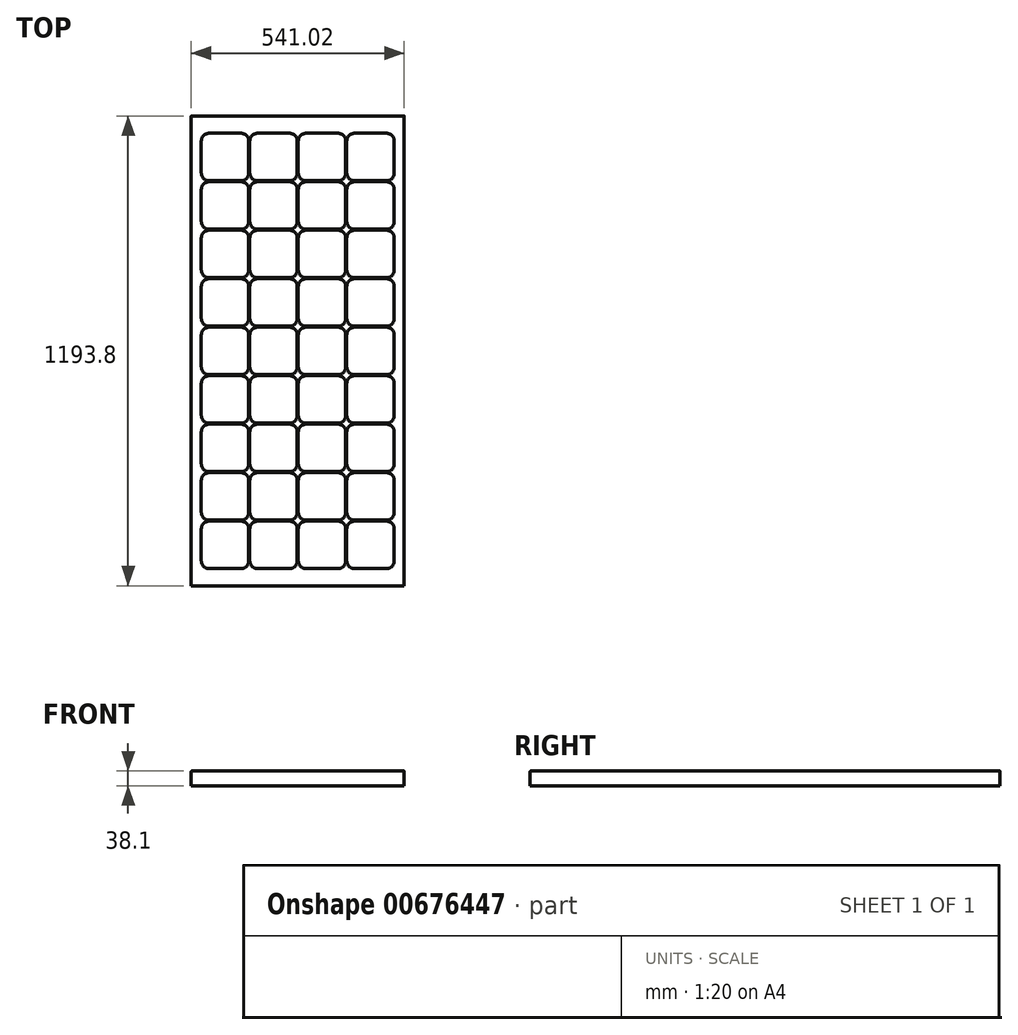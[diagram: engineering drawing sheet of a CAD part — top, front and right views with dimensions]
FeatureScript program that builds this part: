
annotation { "Feature Type Name" : "Feature", "Feature Type Description" : "" }
export const myFeature = defineFeature(function(context is Context, id is Id, definition is map)
    precondition{}
    {
        {
            var Q0;
            Q0=qCreatedBy(makeId("Top.planeOp"),FACE);
            var sketch = newSketch(context, id + "F0", { "sketchPlane" : qUnion([Q0])});
            skLineSegment(sketch, "E0.bottom", {"start": v(270.51, 596.9) * mm, "end": v(-270.5, 596.9) * mm});
            skLineSegment(sketch, "E0.top", {"start": v(270.5, -596.9) * mm, "end": v(-270.51, -596.9) * mm});
            skLineSegment(sketch, "E0.left", {"start": v(270.51, 596.9) * mm, "end": v(270.5, -596.9) * mm});
            skLineSegment(sketch, "E0.right", {"start": v(-270.5, 596.9) * mm, "end": v(-270.51, -596.9) * mm});
            skPoint(sketch, "E0.middle", {"position": v(0, 0) * mm});
            skSolve(sketch);
        }
        {
            var Q0;
            Q0=makeQuery(id+"F0.imprint","IMPRINT",FACE,{"disambiguationData":[TD([[makeQuery(id+"F0.imprint","IMPRINT",EDGE,{"derivedFrom":sQuery(id+"F0.wireOp",EDGE,"E0.bottom")}),1.0]])]});
            extrude(context, id + "F1", {"entities" : qUnion([Q0]), "depth" : 38.1 * mm, "offsetDistance" : 25.4 * mm});
        }
        {
            var Q0;
            Q0=qCreatedBy(makeId("Top.planeOp"),FACE);
            var sketch = newSketch(context, id + "F2", { "sketchPlane" : qUnion([Q0])});
            skLineSegment(sketch, "E1.bottom", {"start": v(-225.1, 553.09) * mm, "end": v(-144.46, 553.09) * mm});
            skLineSegment(sketch, "E1.top", {"start": v(-225.1, 432.44) * mm, "end": v(-144.46, 432.44) * mm});
            skLineSegment(sketch, "E1.left", {"start": v(-245.1, 533.09) * mm, "end": v(-245.1, 452.44) * mm});
            skLineSegment(sketch, "E1.right", {"start": v(-124.46, 533.09) * mm, "end": v(-124.46, 452.44) * mm});
            skPoint(sketch, "E2.visualSharp", {"position": v(-245.1, 553.09) * mm});
            skArc(sketch, "E2.filletArc", {"start": v(-225.1, 553.09) * mm, "mid": v(-239.25, 547.23) * mm, "end": v(-245.1, 533.09) * mm});
            skPoint(sketch, "E3.visualSharp", {"position": v(-124.46, 553.09) * mm});
            skArc(sketch, "E3.filletArc", {"start": v(-124.46, 533.09) * mm, "mid": v(-130.32, 547.23) * mm, "end": v(-144.46, 553.09) * mm});
            skPoint(sketch, "E4.visualSharp", {"position": v(-124.46, 432.44) * mm});
            skArc(sketch, "E4.filletArc", {"start": v(-144.46, 432.44) * mm, "mid": v(-130.32, 438.3) * mm, "end": v(-124.46, 452.44) * mm});
            skPoint(sketch, "E5.visualSharp", {"position": v(-245.1, 432.44) * mm});
            skArc(sketch, "E5.filletArc", {"start": v(-245.1, 452.44) * mm, "mid": v(-239.25, 438.3) * mm, "end": v(-225.1, 432.44) * mm});
            skLineSegment(sketch, "E6.0.1.0", {"start": v(-225.1, 429.9) * mm, "end": v(-144.46, 429.9) * mm});
            skPoint(sketch, "E6.0.1.1", {"position": v(-245.1, 309.25) * mm});
            skPoint(sketch, "E6.0.1.2", {"position": v(-124.46, 309.25) * mm});
            skPoint(sketch, "E6.0.1.3", {"position": v(-124.46, 429.9) * mm});
            skLineSegment(sketch, "E6.0.1.4", {"start": v(-225.1, 309.25) * mm, "end": v(-144.46, 309.25) * mm});
            skLineSegment(sketch, "E6.0.1.5", {"start": v(-245.1, 409.9) * mm, "end": v(-245.1, 329.25) * mm});
            skPoint(sketch, "E6.0.1.6", {"position": v(-245.1, 429.9) * mm});
            skLineSegment(sketch, "E6.0.1.7", {"start": v(-124.46, 409.9) * mm, "end": v(-124.46, 329.25) * mm});
            skArc(sketch, "E6.0.1.8", {"start": v(-124.46, 409.9) * mm, "mid": v(-130.32, 424.04) * mm, "end": v(-144.46, 429.9) * mm});
            skArc(sketch, "E6.0.1.9", {"start": v(-144.46, 309.25) * mm, "mid": v(-130.32, 315.1) * mm, "end": v(-124.46, 329.25) * mm});
            skArc(sketch, "E6.0.1.10", {"start": v(-245.1, 329.25) * mm, "mid": v(-239.25, 315.1) * mm, "end": v(-225.1, 309.25) * mm});
            skArc(sketch, "E6.0.1.11", {"start": v(-225.1, 429.9) * mm, "mid": v(-239.25, 424.04) * mm, "end": v(-245.1, 409.9) * mm});
            skLineSegment(sketch, "E6.0.2.0", {"start": v(-225.1, 306.7) * mm, "end": v(-144.46, 306.7) * mm});
            skPoint(sketch, "E6.0.2.1", {"position": v(-245.1, 186.06) * mm});
            skPoint(sketch, "E6.0.2.2", {"position": v(-124.46, 186.06) * mm});
            skPoint(sketch, "E6.0.2.3", {"position": v(-124.46, 306.7) * mm});
            skLineSegment(sketch, "E6.0.2.4", {"start": v(-225.1, 186.06) * mm, "end": v(-144.46, 186.06) * mm});
            skLineSegment(sketch, "E6.0.2.5", {"start": v(-245.1, 286.7) * mm, "end": v(-245.1, 206.06) * mm});
            skPoint(sketch, "E6.0.2.6", {"position": v(-245.1, 306.7) * mm});
            skLineSegment(sketch, "E6.0.2.7", {"start": v(-124.46, 286.7) * mm, "end": v(-124.46, 206.06) * mm});
            skArc(sketch, "E6.0.2.8", {"start": v(-124.46, 286.7) * mm, "mid": v(-130.32, 300.85) * mm, "end": v(-144.46, 306.7) * mm});
            skArc(sketch, "E6.0.2.9", {"start": v(-144.46, 186.06) * mm, "mid": v(-130.32, 191.91) * mm, "end": v(-124.46, 206.06) * mm});
            skArc(sketch, "E6.0.2.10", {"start": v(-245.1, 206.06) * mm, "mid": v(-239.25, 191.91) * mm, "end": v(-225.1, 186.06) * mm});
            skArc(sketch, "E6.0.2.11", {"start": v(-225.1, 306.7) * mm, "mid": v(-239.25, 300.85) * mm, "end": v(-245.1, 286.7) * mm});
            skLineSegment(sketch, "E6.0.3.0", {"start": v(-225.1, 183.52) * mm, "end": v(-144.46, 183.52) * mm});
            skPoint(sketch, "E6.0.3.1", {"position": v(-245.1, 62.87) * mm});
            skPoint(sketch, "E6.0.3.2", {"position": v(-124.46, 62.87) * mm});
            skPoint(sketch, "E6.0.3.3", {"position": v(-124.46, 183.52) * mm});
            skLineSegment(sketch, "E6.0.3.4", {"start": v(-225.1, 62.87) * mm, "end": v(-144.46, 62.87) * mm});
            skLineSegment(sketch, "E6.0.3.5", {"start": v(-245.1, 163.52) * mm, "end": v(-245.1, 82.87) * mm});
            skPoint(sketch, "E6.0.3.6", {"position": v(-245.1, 183.52) * mm});
            skLineSegment(sketch, "E6.0.3.7", {"start": v(-124.46, 163.52) * mm, "end": v(-124.46, 82.87) * mm});
            skArc(sketch, "E6.0.3.8", {"start": v(-124.46, 163.52) * mm, "mid": v(-130.32, 177.66) * mm, "end": v(-144.46, 183.52) * mm});
            skArc(sketch, "E6.0.3.9", {"start": v(-144.46, 62.87) * mm, "mid": v(-130.32, 68.72) * mm, "end": v(-124.46, 82.87) * mm});
            skArc(sketch, "E6.0.3.10", {"start": v(-245.1, 82.87) * mm, "mid": v(-239.25, 68.72) * mm, "end": v(-225.1, 62.87) * mm});
            skArc(sketch, "E6.0.3.11", {"start": v(-225.1, 183.52) * mm, "mid": v(-239.25, 177.66) * mm, "end": v(-245.1, 163.52) * mm});
            skLineSegment(sketch, "E6.0.4.0", {"start": v(-225.1, 60.33) * mm, "end": v(-144.46, 60.33) * mm});
            skPoint(sketch, "E6.0.4.1", {"position": v(-245.1, -60.32) * mm});
            skPoint(sketch, "E6.0.4.2", {"position": v(-124.46, -60.32) * mm});
            skPoint(sketch, "E6.0.4.3", {"position": v(-124.46, 60.33) * mm});
            skLineSegment(sketch, "E6.0.4.4", {"start": v(-225.1, -60.32) * mm, "end": v(-144.46, -60.32) * mm});
            skLineSegment(sketch, "E6.0.4.5", {"start": v(-245.1, 40.33) * mm, "end": v(-245.1, -40.32) * mm});
            skPoint(sketch, "E6.0.4.6", {"position": v(-245.1, 60.33) * mm});
            skLineSegment(sketch, "E6.0.4.7", {"start": v(-124.46, 40.33) * mm, "end": v(-124.46, -40.32) * mm});
            skArc(sketch, "E6.0.4.8", {"start": v(-124.46, 40.33) * mm, "mid": v(-130.32, 54.47) * mm, "end": v(-144.46, 60.33) * mm});
            skArc(sketch, "E6.0.4.9", {"start": v(-144.46, -60.32) * mm, "mid": v(-130.32, -54.47) * mm, "end": v(-124.46, -40.32) * mm});
            skArc(sketch, "E6.0.4.10", {"start": v(-245.1, -40.32) * mm, "mid": v(-239.25, -54.47) * mm, "end": v(-225.1, -60.32) * mm});
            skArc(sketch, "E6.0.4.11", {"start": v(-225.1, 60.33) * mm, "mid": v(-239.25, 54.47) * mm, "end": v(-245.1, 40.33) * mm});
            skLineSegment(sketch, "E6.0.5.0", {"start": v(-225.1, -62.86) * mm, "end": v(-144.46, -62.86) * mm});
            skPoint(sketch, "E6.0.5.1", {"position": v(-245.1, -183.51) * mm});
            skPoint(sketch, "E6.0.5.2", {"position": v(-124.46, -183.51) * mm});
            skPoint(sketch, "E6.0.5.3", {"position": v(-124.46, -62.86) * mm});
            skLineSegment(sketch, "E6.0.5.4", {"start": v(-225.1, -183.51) * mm, "end": v(-144.46, -183.51) * mm});
            skLineSegment(sketch, "E6.0.5.5", {"start": v(-245.1, -82.86) * mm, "end": v(-245.1, -163.51) * mm});
            skPoint(sketch, "E6.0.5.6", {"position": v(-245.1, -62.86) * mm});
            skLineSegment(sketch, "E6.0.5.7", {"start": v(-124.46, -82.86) * mm, "end": v(-124.46, -163.51) * mm});
            skArc(sketch, "E6.0.5.8", {"start": v(-124.46, -82.86) * mm, "mid": v(-130.32, -68.72) * mm, "end": v(-144.46, -62.86) * mm});
            skArc(sketch, "E6.0.5.9", {"start": v(-144.46, -183.51) * mm, "mid": v(-130.32, -177.66) * mm, "end": v(-124.46, -163.51) * mm});
            skArc(sketch, "E6.0.5.10", {"start": v(-245.1, -163.51) * mm, "mid": v(-239.25, -177.66) * mm, "end": v(-225.1, -183.51) * mm});
            skArc(sketch, "E6.0.5.11", {"start": v(-225.1, -62.86) * mm, "mid": v(-239.25, -68.72) * mm, "end": v(-245.1, -82.86) * mm});
            skLineSegment(sketch, "E6.0.6.0", {"start": v(-225.1, -186.05) * mm, "end": v(-144.46, -186.05) * mm});
            skPoint(sketch, "E6.0.6.1", {"position": v(-245.1, -306.7) * mm});
            skPoint(sketch, "E6.0.6.2", {"position": v(-124.46, -306.7) * mm});
            skPoint(sketch, "E6.0.6.3", {"position": v(-124.46, -186.05) * mm});
            skLineSegment(sketch, "E6.0.6.4", {"start": v(-225.1, -306.7) * mm, "end": v(-144.46, -306.7) * mm});
            skLineSegment(sketch, "E6.0.6.5", {"start": v(-245.1, -206.05) * mm, "end": v(-245.1, -286.7) * mm});
            skPoint(sketch, "E6.0.6.6", {"position": v(-245.1, -186.05) * mm});
            skLineSegment(sketch, "E6.0.6.7", {"start": v(-124.46, -206.05) * mm, "end": v(-124.46, -286.7) * mm});
            skArc(sketch, "E6.0.6.8", {"start": v(-124.46, -206.05) * mm, "mid": v(-130.32, -191.91) * mm, "end": v(-144.46, -186.05) * mm});
            skArc(sketch, "E6.0.6.9", {"start": v(-144.46, -306.7) * mm, "mid": v(-130.32, -300.85) * mm, "end": v(-124.46, -286.7) * mm});
            skArc(sketch, "E6.0.6.10", {"start": v(-245.1, -286.7) * mm, "mid": v(-239.25, -300.85) * mm, "end": v(-225.1, -306.7) * mm});
            skArc(sketch, "E6.0.6.11", {"start": v(-225.1, -186.05) * mm, "mid": v(-239.25, -191.91) * mm, "end": v(-245.1, -206.05) * mm});
            skLineSegment(sketch, "E6.0.7.0", {"start": v(-225.1, -309.24) * mm, "end": v(-144.46, -309.24) * mm});
            skPoint(sketch, "E6.0.7.1", {"position": v(-245.1, -429.9) * mm});
            skPoint(sketch, "E6.0.7.2", {"position": v(-124.46, -429.9) * mm});
            skPoint(sketch, "E6.0.7.3", {"position": v(-124.46, -309.24) * mm});
            skLineSegment(sketch, "E6.0.7.4", {"start": v(-225.1, -429.9) * mm, "end": v(-144.46, -429.9) * mm});
            skLineSegment(sketch, "E6.0.7.5", {"start": v(-245.1, -329.24) * mm, "end": v(-245.1, -409.9) * mm});
            skPoint(sketch, "E6.0.7.6", {"position": v(-245.1, -309.24) * mm});
            skLineSegment(sketch, "E6.0.7.7", {"start": v(-124.46, -329.24) * mm, "end": v(-124.46, -409.9) * mm});
            skArc(sketch, "E6.0.7.8", {"start": v(-124.46, -329.24) * mm, "mid": v(-130.32, -315.1) * mm, "end": v(-144.46, -309.24) * mm});
            skArc(sketch, "E6.0.7.9", {"start": v(-144.46, -429.9) * mm, "mid": v(-130.32, -424.04) * mm, "end": v(-124.46, -409.9) * mm});
            skArc(sketch, "E6.0.7.10", {"start": v(-245.1, -409.9) * mm, "mid": v(-239.25, -424.04) * mm, "end": v(-225.1, -429.9) * mm});
            skArc(sketch, "E6.0.7.11", {"start": v(-225.1, -309.24) * mm, "mid": v(-239.25, -315.1) * mm, "end": v(-245.1, -329.24) * mm});
            skLineSegment(sketch, "E6.0.8.0", {"start": v(-225.1, -432.43) * mm, "end": v(-144.46, -432.43) * mm});
            skPoint(sketch, "E6.0.8.1", {"position": v(-245.1, -553.08) * mm});
            skPoint(sketch, "E6.0.8.2", {"position": v(-124.46, -553.08) * mm});
            skPoint(sketch, "E6.0.8.3", {"position": v(-124.46, -432.43) * mm});
            skLineSegment(sketch, "E6.0.8.4", {"start": v(-225.1, -553.08) * mm, "end": v(-144.46, -553.08) * mm});
            skLineSegment(sketch, "E6.0.8.5", {"start": v(-245.1, -452.43) * mm, "end": v(-245.1, -533.08) * mm});
            skPoint(sketch, "E6.0.8.6", {"position": v(-245.1, -432.43) * mm});
            skLineSegment(sketch, "E6.0.8.7", {"start": v(-124.46, -452.43) * mm, "end": v(-124.46, -533.08) * mm});
            skArc(sketch, "E6.0.8.8", {"start": v(-124.46, -452.43) * mm, "mid": v(-130.32, -438.3) * mm, "end": v(-144.46, -432.43) * mm});
            skArc(sketch, "E6.0.8.9", {"start": v(-144.46, -553.08) * mm, "mid": v(-130.32, -547.23) * mm, "end": v(-124.46, -533.08) * mm});
            skArc(sketch, "E6.0.8.10", {"start": v(-245.1, -533.08) * mm, "mid": v(-239.25, -547.23) * mm, "end": v(-225.1, -553.08) * mm});
            skArc(sketch, "E6.0.8.11", {"start": v(-225.1, -432.43) * mm, "mid": v(-239.25, -438.3) * mm, "end": v(-245.1, -452.43) * mm});
            skLineSegment(sketch, "E6.1.0.0", {"start": v(-101.92, 553.09) * mm, "end": v(-21.27, 553.09) * mm});
            skPoint(sketch, "E6.1.0.1", {"position": v(-121.92, 432.44) * mm});
            skPoint(sketch, "E6.1.0.2", {"position": v(-1.27, 432.44) * mm});
            skPoint(sketch, "E6.1.0.3", {"position": v(-1.27, 553.09) * mm});
            skLineSegment(sketch, "E6.1.0.4", {"start": v(-101.92, 432.44) * mm, "end": v(-21.27, 432.44) * mm});
            skLineSegment(sketch, "E6.1.0.5", {"start": v(-121.92, 533.09) * mm, "end": v(-121.92, 452.44) * mm});
            skPoint(sketch, "E6.1.0.6", {"position": v(-121.92, 553.09) * mm});
            skLineSegment(sketch, "E6.1.0.7", {"start": v(-1.27, 533.09) * mm, "end": v(-1.27, 452.44) * mm});
            skArc(sketch, "E6.1.0.8", {"start": v(-1.27, 533.09) * mm, "mid": v(-7.13, 547.23) * mm, "end": v(-21.27, 553.09) * mm});
            skArc(sketch, "E6.1.0.9", {"start": v(-21.27, 432.44) * mm, "mid": v(-7.13, 438.3) * mm, "end": v(-1.27, 452.44) * mm});
            skArc(sketch, "E6.1.0.10", {"start": v(-121.92, 452.44) * mm, "mid": v(-116.06, 438.3) * mm, "end": v(-101.92, 432.44) * mm});
            skArc(sketch, "E6.1.0.11", {"start": v(-101.92, 553.09) * mm, "mid": v(-116.06, 547.23) * mm, "end": v(-121.92, 533.09) * mm});
            skLineSegment(sketch, "E6.1.1.0", {"start": v(-101.92, 429.9) * mm, "end": v(-21.27, 429.9) * mm});
            skPoint(sketch, "E6.1.1.1", {"position": v(-121.92, 309.25) * mm});
            skPoint(sketch, "E6.1.1.2", {"position": v(-1.27, 309.25) * mm});
            skPoint(sketch, "E6.1.1.3", {"position": v(-1.27, 429.9) * mm});
            skLineSegment(sketch, "E6.1.1.4", {"start": v(-101.92, 309.25) * mm, "end": v(-21.27, 309.25) * mm});
            skLineSegment(sketch, "E6.1.1.5", {"start": v(-121.92, 409.9) * mm, "end": v(-121.92, 329.25) * mm});
            skPoint(sketch, "E6.1.1.6", {"position": v(-121.92, 429.9) * mm});
            skLineSegment(sketch, "E6.1.1.7", {"start": v(-1.27, 409.9) * mm, "end": v(-1.27, 329.25) * mm});
            skArc(sketch, "E6.1.1.8", {"start": v(-1.27, 409.9) * mm, "mid": v(-7.13, 424.04) * mm, "end": v(-21.27, 429.9) * mm});
            skArc(sketch, "E6.1.1.9", {"start": v(-21.27, 309.25) * mm, "mid": v(-7.13, 315.1) * mm, "end": v(-1.27, 329.25) * mm});
            skArc(sketch, "E6.1.1.10", {"start": v(-121.92, 329.25) * mm, "mid": v(-116.06, 315.1) * mm, "end": v(-101.92, 309.25) * mm});
            skArc(sketch, "E6.1.1.11", {"start": v(-101.92, 429.9) * mm, "mid": v(-116.06, 424.04) * mm, "end": v(-121.92, 409.9) * mm});
            skLineSegment(sketch, "E6.1.2.0", {"start": v(-101.92, 306.7) * mm, "end": v(-21.27, 306.7) * mm});
            skPoint(sketch, "E6.1.2.1", {"position": v(-121.92, 186.06) * mm});
            skPoint(sketch, "E6.1.2.2", {"position": v(-1.27, 186.06) * mm});
            skPoint(sketch, "E6.1.2.3", {"position": v(-1.27, 306.7) * mm});
            skLineSegment(sketch, "E6.1.2.4", {"start": v(-101.92, 186.06) * mm, "end": v(-21.27, 186.06) * mm});
            skLineSegment(sketch, "E6.1.2.5", {"start": v(-121.92, 286.7) * mm, "end": v(-121.92, 206.06) * mm});
            skPoint(sketch, "E6.1.2.6", {"position": v(-121.92, 306.7) * mm});
            skLineSegment(sketch, "E6.1.2.7", {"start": v(-1.27, 286.7) * mm, "end": v(-1.27, 206.06) * mm});
            skArc(sketch, "E6.1.2.8", {"start": v(-1.27, 286.7) * mm, "mid": v(-7.13, 300.85) * mm, "end": v(-21.27, 306.7) * mm});
            skArc(sketch, "E6.1.2.9", {"start": v(-21.27, 186.06) * mm, "mid": v(-7.13, 191.91) * mm, "end": v(-1.27, 206.06) * mm});
            skArc(sketch, "E6.1.2.10", {"start": v(-121.92, 206.06) * mm, "mid": v(-116.06, 191.91) * mm, "end": v(-101.92, 186.06) * mm});
            skArc(sketch, "E6.1.2.11", {"start": v(-101.92, 306.7) * mm, "mid": v(-116.06, 300.85) * mm, "end": v(-121.92, 286.7) * mm});
            skLineSegment(sketch, "E6.1.3.0", {"start": v(-101.92, 183.52) * mm, "end": v(-21.27, 183.52) * mm});
            skPoint(sketch, "E6.1.3.1", {"position": v(-121.92, 62.87) * mm});
            skPoint(sketch, "E6.1.3.2", {"position": v(-1.27, 62.87) * mm});
            skPoint(sketch, "E6.1.3.3", {"position": v(-1.27, 183.52) * mm});
            skLineSegment(sketch, "E6.1.3.4", {"start": v(-101.92, 62.87) * mm, "end": v(-21.27, 62.87) * mm});
            skLineSegment(sketch, "E6.1.3.5", {"start": v(-121.92, 163.52) * mm, "end": v(-121.92, 82.87) * mm});
            skPoint(sketch, "E6.1.3.6", {"position": v(-121.92, 183.52) * mm});
            skLineSegment(sketch, "E6.1.3.7", {"start": v(-1.27, 163.52) * mm, "end": v(-1.27, 82.87) * mm});
            skArc(sketch, "E6.1.3.8", {"start": v(-1.27, 163.52) * mm, "mid": v(-7.13, 177.66) * mm, "end": v(-21.27, 183.52) * mm});
            skArc(sketch, "E6.1.3.9", {"start": v(-21.27, 62.87) * mm, "mid": v(-7.13, 68.72) * mm, "end": v(-1.27, 82.87) * mm});
            skArc(sketch, "E6.1.3.10", {"start": v(-121.92, 82.87) * mm, "mid": v(-116.06, 68.72) * mm, "end": v(-101.92, 62.87) * mm});
            skArc(sketch, "E6.1.3.11", {"start": v(-101.92, 183.52) * mm, "mid": v(-116.06, 177.66) * mm, "end": v(-121.92, 163.52) * mm});
            skLineSegment(sketch, "E6.1.4.0", {"start": v(-101.92, 60.33) * mm, "end": v(-21.27, 60.33) * mm});
            skPoint(sketch, "E6.1.4.1", {"position": v(-121.92, -60.32) * mm});
            skPoint(sketch, "E6.1.4.2", {"position": v(-1.27, -60.32) * mm});
            skPoint(sketch, "E6.1.4.3", {"position": v(-1.27, 60.33) * mm});
            skLineSegment(sketch, "E6.1.4.4", {"start": v(-101.92, -60.32) * mm, "end": v(-21.27, -60.32) * mm});
            skLineSegment(sketch, "E6.1.4.5", {"start": v(-121.92, 40.33) * mm, "end": v(-121.92, -40.32) * mm});
            skPoint(sketch, "E6.1.4.6", {"position": v(-121.92, 60.33) * mm});
            skLineSegment(sketch, "E6.1.4.7", {"start": v(-1.27, 40.33) * mm, "end": v(-1.27, -40.32) * mm});
            skArc(sketch, "E6.1.4.8", {"start": v(-1.27, 40.33) * mm, "mid": v(-7.13, 54.47) * mm, "end": v(-21.27, 60.33) * mm});
            skArc(sketch, "E6.1.4.9", {"start": v(-21.27, -60.32) * mm, "mid": v(-7.13, -54.47) * mm, "end": v(-1.27, -40.32) * mm});
            skArc(sketch, "E6.1.4.10", {"start": v(-121.92, -40.32) * mm, "mid": v(-116.06, -54.47) * mm, "end": v(-101.92, -60.32) * mm});
            skArc(sketch, "E6.1.4.11", {"start": v(-101.92, 60.33) * mm, "mid": v(-116.06, 54.47) * mm, "end": v(-121.92, 40.33) * mm});
            skLineSegment(sketch, "E6.1.5.0", {"start": v(-101.92, -62.86) * mm, "end": v(-21.27, -62.86) * mm});
            skPoint(sketch, "E6.1.5.1", {"position": v(-121.92, -183.51) * mm});
            skPoint(sketch, "E6.1.5.2", {"position": v(-1.27, -183.51) * mm});
            skPoint(sketch, "E6.1.5.3", {"position": v(-1.27, -62.86) * mm});
            skLineSegment(sketch, "E6.1.5.4", {"start": v(-101.92, -183.51) * mm, "end": v(-21.27, -183.51) * mm});
            skLineSegment(sketch, "E6.1.5.5", {"start": v(-121.92, -82.86) * mm, "end": v(-121.92, -163.51) * mm});
            skPoint(sketch, "E6.1.5.6", {"position": v(-121.92, -62.86) * mm});
            skLineSegment(sketch, "E6.1.5.7", {"start": v(-1.27, -82.86) * mm, "end": v(-1.27, -163.51) * mm});
            skArc(sketch, "E6.1.5.8", {"start": v(-1.27, -82.86) * mm, "mid": v(-7.13, -68.72) * mm, "end": v(-21.27, -62.86) * mm});
            skArc(sketch, "E6.1.5.9", {"start": v(-21.27, -183.51) * mm, "mid": v(-7.13, -177.66) * mm, "end": v(-1.27, -163.51) * mm});
            skArc(sketch, "E6.1.5.10", {"start": v(-121.92, -163.51) * mm, "mid": v(-116.06, -177.66) * mm, "end": v(-101.92, -183.51) * mm});
            skArc(sketch, "E6.1.5.11", {"start": v(-101.92, -62.86) * mm, "mid": v(-116.06, -68.72) * mm, "end": v(-121.92, -82.86) * mm});
            skLineSegment(sketch, "E6.1.6.0", {"start": v(-101.92, -186.05) * mm, "end": v(-21.27, -186.05) * mm});
            skPoint(sketch, "E6.1.6.1", {"position": v(-121.92, -306.7) * mm});
            skPoint(sketch, "E6.1.6.2", {"position": v(-1.27, -306.7) * mm});
            skPoint(sketch, "E6.1.6.3", {"position": v(-1.27, -186.05) * mm});
            skLineSegment(sketch, "E6.1.6.4", {"start": v(-101.92, -306.7) * mm, "end": v(-21.27, -306.7) * mm});
            skLineSegment(sketch, "E6.1.6.5", {"start": v(-121.92, -206.05) * mm, "end": v(-121.92, -286.7) * mm});
            skPoint(sketch, "E6.1.6.6", {"position": v(-121.92, -186.05) * mm});
            skLineSegment(sketch, "E6.1.6.7", {"start": v(-1.27, -206.05) * mm, "end": v(-1.27, -286.7) * mm});
            skArc(sketch, "E6.1.6.8", {"start": v(-1.27, -206.05) * mm, "mid": v(-7.13, -191.91) * mm, "end": v(-21.27, -186.05) * mm});
            skArc(sketch, "E6.1.6.9", {"start": v(-21.27, -306.7) * mm, "mid": v(-7.13, -300.85) * mm, "end": v(-1.27, -286.7) * mm});
            skArc(sketch, "E6.1.6.10", {"start": v(-121.92, -286.7) * mm, "mid": v(-116.06, -300.85) * mm, "end": v(-101.92, -306.7) * mm});
            skArc(sketch, "E6.1.6.11", {"start": v(-101.92, -186.05) * mm, "mid": v(-116.06, -191.91) * mm, "end": v(-121.92, -206.05) * mm});
            skLineSegment(sketch, "E6.1.7.0", {"start": v(-101.92, -309.24) * mm, "end": v(-21.27, -309.24) * mm});
            skPoint(sketch, "E6.1.7.1", {"position": v(-121.92, -429.9) * mm});
            skPoint(sketch, "E6.1.7.2", {"position": v(-1.27, -429.9) * mm});
            skPoint(sketch, "E6.1.7.3", {"position": v(-1.27, -309.24) * mm});
            skLineSegment(sketch, "E6.1.7.4", {"start": v(-101.92, -429.9) * mm, "end": v(-21.27, -429.9) * mm});
            skLineSegment(sketch, "E6.1.7.5", {"start": v(-121.92, -329.24) * mm, "end": v(-121.92, -409.9) * mm});
            skPoint(sketch, "E6.1.7.6", {"position": v(-121.92, -309.24) * mm});
            skLineSegment(sketch, "E6.1.7.7", {"start": v(-1.27, -329.24) * mm, "end": v(-1.27, -409.9) * mm});
            skArc(sketch, "E6.1.7.8", {"start": v(-1.27, -329.24) * mm, "mid": v(-7.13, -315.1) * mm, "end": v(-21.27, -309.24) * mm});
            skArc(sketch, "E6.1.7.9", {"start": v(-21.27, -429.9) * mm, "mid": v(-7.13, -424.04) * mm, "end": v(-1.27, -409.9) * mm});
            skArc(sketch, "E6.1.7.10", {"start": v(-121.92, -409.9) * mm, "mid": v(-116.06, -424.04) * mm, "end": v(-101.92, -429.9) * mm});
            skArc(sketch, "E6.1.7.11", {"start": v(-101.92, -309.24) * mm, "mid": v(-116.06, -315.1) * mm, "end": v(-121.92, -329.24) * mm});
            skLineSegment(sketch, "E6.1.8.0", {"start": v(-101.92, -432.43) * mm, "end": v(-21.27, -432.43) * mm});
            skPoint(sketch, "E6.1.8.1", {"position": v(-121.92, -553.08) * mm});
            skPoint(sketch, "E6.1.8.2", {"position": v(-1.27, -553.08) * mm});
            skPoint(sketch, "E6.1.8.3", {"position": v(-1.27, -432.43) * mm});
            skLineSegment(sketch, "E6.1.8.4", {"start": v(-101.92, -553.08) * mm, "end": v(-21.27, -553.08) * mm});
            skLineSegment(sketch, "E6.1.8.5", {"start": v(-121.92, -452.43) * mm, "end": v(-121.92, -533.08) * mm});
            skPoint(sketch, "E6.1.8.6", {"position": v(-121.92, -432.43) * mm});
            skLineSegment(sketch, "E6.1.8.7", {"start": v(-1.27, -452.43) * mm, "end": v(-1.27, -533.08) * mm});
            skArc(sketch, "E6.1.8.8", {"start": v(-1.27, -452.43) * mm, "mid": v(-7.13, -438.3) * mm, "end": v(-21.27, -432.43) * mm});
            skArc(sketch, "E6.1.8.9", {"start": v(-21.27, -553.08) * mm, "mid": v(-7.13, -547.23) * mm, "end": v(-1.27, -533.08) * mm});
            skArc(sketch, "E6.1.8.10", {"start": v(-121.92, -533.08) * mm, "mid": v(-116.06, -547.23) * mm, "end": v(-101.92, -553.08) * mm});
            skArc(sketch, "E6.1.8.11", {"start": v(-101.92, -432.43) * mm, "mid": v(-116.06, -438.3) * mm, "end": v(-121.92, -452.43) * mm});
            skLineSegment(sketch, "E6.2.0.0", {"start": v(21.27, 553.08) * mm, "end": v(101.92, 553.08) * mm});
            skPoint(sketch, "E6.2.0.1", {"position": v(1.27, 432.44) * mm});
            skPoint(sketch, "E6.2.0.2", {"position": v(121.92, 432.44) * mm});
            skPoint(sketch, "E6.2.0.3", {"position": v(121.92, 553.08) * mm});
            skLineSegment(sketch, "E6.2.0.4", {"start": v(21.27, 432.44) * mm, "end": v(101.92, 432.44) * mm});
            skLineSegment(sketch, "E6.2.0.5", {"start": v(1.27, 533.09) * mm, "end": v(1.27, 452.44) * mm});
            skPoint(sketch, "E6.2.0.6", {"position": v(1.27, 553.08) * mm});
            skLineSegment(sketch, "E6.2.0.7", {"start": v(121.92, 533.08) * mm, "end": v(121.92, 452.44) * mm});
            skArc(sketch, "E6.2.0.8", {"start": v(121.92, 533.08) * mm, "mid": v(116.06, 547.23) * mm, "end": v(101.92, 553.08) * mm});
            skArc(sketch, "E6.2.0.9", {"start": v(101.92, 432.44) * mm, "mid": v(116.06, 438.3) * mm, "end": v(121.92, 452.44) * mm});
            skArc(sketch, "E6.2.0.10", {"start": v(1.27, 452.44) * mm, "mid": v(7.13, 438.3) * mm, "end": v(21.27, 432.44) * mm});
            skArc(sketch, "E6.2.0.11", {"start": v(21.27, 553.09) * mm, "mid": v(7.13, 547.23) * mm, "end": v(1.27, 533.09) * mm});
            skLineSegment(sketch, "E6.2.1.0", {"start": v(21.27, 429.9) * mm, "end": v(101.92, 429.9) * mm});
            skPoint(sketch, "E6.2.1.1", {"position": v(1.27, 309.25) * mm});
            skPoint(sketch, "E6.2.1.2", {"position": v(121.92, 309.25) * mm});
            skPoint(sketch, "E6.2.1.3", {"position": v(121.92, 429.9) * mm});
            skLineSegment(sketch, "E6.2.1.4", {"start": v(21.27, 309.25) * mm, "end": v(101.92, 309.25) * mm});
            skLineSegment(sketch, "E6.2.1.5", {"start": v(1.27, 409.9) * mm, "end": v(1.27, 329.25) * mm});
            skPoint(sketch, "E6.2.1.6", {"position": v(1.27, 429.9) * mm});
            skLineSegment(sketch, "E6.2.1.7", {"start": v(121.92, 409.9) * mm, "end": v(121.92, 329.25) * mm});
            skArc(sketch, "E6.2.1.8", {"start": v(121.92, 409.9) * mm, "mid": v(116.06, 424.04) * mm, "end": v(101.92, 429.9) * mm});
            skArc(sketch, "E6.2.1.9", {"start": v(101.92, 309.25) * mm, "mid": v(116.06, 315.1) * mm, "end": v(121.92, 329.25) * mm});
            skArc(sketch, "E6.2.1.10", {"start": v(1.27, 329.25) * mm, "mid": v(7.13, 315.1) * mm, "end": v(21.27, 309.25) * mm});
            skArc(sketch, "E6.2.1.11", {"start": v(21.27, 429.9) * mm, "mid": v(7.13, 424.04) * mm, "end": v(1.27, 409.9) * mm});
            skLineSegment(sketch, "E6.2.2.0", {"start": v(21.27, 306.7) * mm, "end": v(101.92, 306.7) * mm});
            skPoint(sketch, "E6.2.2.1", {"position": v(1.27, 186.06) * mm});
            skPoint(sketch, "E6.2.2.2", {"position": v(121.92, 186.06) * mm});
            skPoint(sketch, "E6.2.2.3", {"position": v(121.92, 306.7) * mm});
            skLineSegment(sketch, "E6.2.2.4", {"start": v(21.27, 186.06) * mm, "end": v(101.92, 186.06) * mm});
            skLineSegment(sketch, "E6.2.2.5", {"start": v(1.27, 286.7) * mm, "end": v(1.27, 206.06) * mm});
            skPoint(sketch, "E6.2.2.6", {"position": v(1.27, 306.7) * mm});
            skLineSegment(sketch, "E6.2.2.7", {"start": v(121.92, 286.7) * mm, "end": v(121.92, 206.06) * mm});
            skArc(sketch, "E6.2.2.8", {"start": v(121.92, 286.7) * mm, "mid": v(116.06, 300.85) * mm, "end": v(101.92, 306.7) * mm});
            skArc(sketch, "E6.2.2.9", {"start": v(101.92, 186.06) * mm, "mid": v(116.06, 191.91) * mm, "end": v(121.92, 206.06) * mm});
            skArc(sketch, "E6.2.2.10", {"start": v(1.27, 206.06) * mm, "mid": v(7.13, 191.91) * mm, "end": v(21.27, 186.06) * mm});
            skArc(sketch, "E6.2.2.11", {"start": v(21.27, 306.7) * mm, "mid": v(7.13, 300.85) * mm, "end": v(1.27, 286.7) * mm});
            skLineSegment(sketch, "E6.2.3.0", {"start": v(21.27, 183.52) * mm, "end": v(101.92, 183.52) * mm});
            skPoint(sketch, "E6.2.3.1", {"position": v(1.27, 62.87) * mm});
            skPoint(sketch, "E6.2.3.2", {"position": v(121.92, 62.87) * mm});
            skPoint(sketch, "E6.2.3.3", {"position": v(121.92, 183.52) * mm});
            skLineSegment(sketch, "E6.2.3.4", {"start": v(21.27, 62.87) * mm, "end": v(101.92, 62.87) * mm});
            skLineSegment(sketch, "E6.2.3.5", {"start": v(1.27, 163.52) * mm, "end": v(1.27, 82.87) * mm});
            skPoint(sketch, "E6.2.3.6", {"position": v(1.27, 183.52) * mm});
            skLineSegment(sketch, "E6.2.3.7", {"start": v(121.92, 163.52) * mm, "end": v(121.92, 82.87) * mm});
            skArc(sketch, "E6.2.3.8", {"start": v(121.92, 163.52) * mm, "mid": v(116.06, 177.66) * mm, "end": v(101.92, 183.52) * mm});
            skArc(sketch, "E6.2.3.9", {"start": v(101.92, 62.87) * mm, "mid": v(116.06, 68.72) * mm, "end": v(121.92, 82.87) * mm});
            skArc(sketch, "E6.2.3.10", {"start": v(1.27, 82.87) * mm, "mid": v(7.13, 68.72) * mm, "end": v(21.27, 62.87) * mm});
            skArc(sketch, "E6.2.3.11", {"start": v(21.27, 183.52) * mm, "mid": v(7.13, 177.66) * mm, "end": v(1.27, 163.52) * mm});
            skLineSegment(sketch, "E6.2.4.0", {"start": v(21.27, 60.33) * mm, "end": v(101.92, 60.33) * mm});
            skPoint(sketch, "E6.2.4.1", {"position": v(1.27, -60.32) * mm});
            skPoint(sketch, "E6.2.4.2", {"position": v(121.92, -60.32) * mm});
            skPoint(sketch, "E6.2.4.3", {"position": v(121.92, 60.33) * mm});
            skLineSegment(sketch, "E6.2.4.4", {"start": v(21.27, -60.32) * mm, "end": v(101.92, -60.32) * mm});
            skLineSegment(sketch, "E6.2.4.5", {"start": v(1.27, 40.33) * mm, "end": v(1.27, -40.32) * mm});
            skPoint(sketch, "E6.2.4.6", {"position": v(1.27, 60.33) * mm});
            skLineSegment(sketch, "E6.2.4.7", {"start": v(121.92, 40.33) * mm, "end": v(121.92, -40.32) * mm});
            skArc(sketch, "E6.2.4.8", {"start": v(121.92, 40.33) * mm, "mid": v(116.06, 54.47) * mm, "end": v(101.92, 60.33) * mm});
            skArc(sketch, "E6.2.4.9", {"start": v(101.92, -60.32) * mm, "mid": v(116.06, -54.47) * mm, "end": v(121.92, -40.32) * mm});
            skArc(sketch, "E6.2.4.10", {"start": v(1.27, -40.32) * mm, "mid": v(7.13, -54.47) * mm, "end": v(21.27, -60.32) * mm});
            skArc(sketch, "E6.2.4.11", {"start": v(21.27, 60.33) * mm, "mid": v(7.13, 54.47) * mm, "end": v(1.27, 40.33) * mm});
            skLineSegment(sketch, "E6.2.5.0", {"start": v(21.27, -62.86) * mm, "end": v(101.92, -62.86) * mm});
            skPoint(sketch, "E6.2.5.1", {"position": v(1.27, -183.51) * mm});
            skPoint(sketch, "E6.2.5.2", {"position": v(121.92, -183.51) * mm});
            skPoint(sketch, "E6.2.5.3", {"position": v(121.92, -62.86) * mm});
            skLineSegment(sketch, "E6.2.5.4", {"start": v(21.27, -183.51) * mm, "end": v(101.92, -183.51) * mm});
            skLineSegment(sketch, "E6.2.5.5", {"start": v(1.27, -82.86) * mm, "end": v(1.27, -163.51) * mm});
            skPoint(sketch, "E6.2.5.6", {"position": v(1.27, -62.86) * mm});
            skLineSegment(sketch, "E6.2.5.7", {"start": v(121.92, -82.86) * mm, "end": v(121.92, -163.51) * mm});
            skArc(sketch, "E6.2.5.8", {"start": v(121.92, -82.86) * mm, "mid": v(116.06, -68.72) * mm, "end": v(101.92, -62.86) * mm});
            skArc(sketch, "E6.2.5.9", {"start": v(101.92, -183.51) * mm, "mid": v(116.06, -177.66) * mm, "end": v(121.92, -163.51) * mm});
            skArc(sketch, "E6.2.5.10", {"start": v(1.27, -163.51) * mm, "mid": v(7.13, -177.66) * mm, "end": v(21.27, -183.51) * mm});
            skArc(sketch, "E6.2.5.11", {"start": v(21.27, -62.86) * mm, "mid": v(7.13, -68.72) * mm, "end": v(1.27, -82.86) * mm});
            skLineSegment(sketch, "E6.2.6.0", {"start": v(21.27, -186.05) * mm, "end": v(101.92, -186.05) * mm});
            skPoint(sketch, "E6.2.6.1", {"position": v(1.27, -306.7) * mm});
            skPoint(sketch, "E6.2.6.2", {"position": v(121.92, -306.7) * mm});
            skPoint(sketch, "E6.2.6.3", {"position": v(121.92, -186.05) * mm});
            skLineSegment(sketch, "E6.2.6.4", {"start": v(21.27, -306.7) * mm, "end": v(101.92, -306.7) * mm});
            skLineSegment(sketch, "E6.2.6.5", {"start": v(1.27, -206.05) * mm, "end": v(1.27, -286.7) * mm});
            skPoint(sketch, "E6.2.6.6", {"position": v(1.27, -186.05) * mm});
            skLineSegment(sketch, "E6.2.6.7", {"start": v(121.92, -206.05) * mm, "end": v(121.92, -286.7) * mm});
            skArc(sketch, "E6.2.6.8", {"start": v(121.92, -206.05) * mm, "mid": v(116.06, -191.91) * mm, "end": v(101.92, -186.05) * mm});
            skArc(sketch, "E6.2.6.9", {"start": v(101.92, -306.7) * mm, "mid": v(116.06, -300.85) * mm, "end": v(121.92, -286.7) * mm});
            skArc(sketch, "E6.2.6.10", {"start": v(1.27, -286.7) * mm, "mid": v(7.13, -300.85) * mm, "end": v(21.27, -306.7) * mm});
            skArc(sketch, "E6.2.6.11", {"start": v(21.27, -186.05) * mm, "mid": v(7.13, -191.91) * mm, "end": v(1.27, -206.05) * mm});
            skLineSegment(sketch, "E6.2.7.0", {"start": v(21.27, -309.24) * mm, "end": v(101.92, -309.24) * mm});
            skPoint(sketch, "E6.2.7.1", {"position": v(1.27, -429.9) * mm});
            skPoint(sketch, "E6.2.7.2", {"position": v(121.92, -429.9) * mm});
            skPoint(sketch, "E6.2.7.3", {"position": v(121.92, -309.24) * mm});
            skLineSegment(sketch, "E6.2.7.4", {"start": v(21.27, -429.9) * mm, "end": v(101.92, -429.9) * mm});
            skLineSegment(sketch, "E6.2.7.5", {"start": v(1.27, -329.24) * mm, "end": v(1.27, -409.9) * mm});
            skPoint(sketch, "E6.2.7.6", {"position": v(1.27, -309.24) * mm});
            skLineSegment(sketch, "E6.2.7.7", {"start": v(121.92, -329.24) * mm, "end": v(121.92, -409.9) * mm});
            skArc(sketch, "E6.2.7.8", {"start": v(121.92, -329.24) * mm, "mid": v(116.06, -315.1) * mm, "end": v(101.92, -309.24) * mm});
            skArc(sketch, "E6.2.7.9", {"start": v(101.92, -429.9) * mm, "mid": v(116.06, -424.04) * mm, "end": v(121.92, -409.9) * mm});
            skArc(sketch, "E6.2.7.10", {"start": v(1.27, -409.9) * mm, "mid": v(7.13, -424.04) * mm, "end": v(21.27, -429.9) * mm});
            skArc(sketch, "E6.2.7.11", {"start": v(21.27, -309.24) * mm, "mid": v(7.13, -315.1) * mm, "end": v(1.27, -329.24) * mm});
            skLineSegment(sketch, "E6.2.8.0", {"start": v(21.27, -432.43) * mm, "end": v(101.92, -432.43) * mm});
            skPoint(sketch, "E6.2.8.1", {"position": v(1.27, -553.08) * mm});
            skPoint(sketch, "E6.2.8.2", {"position": v(121.92, -553.08) * mm});
            skPoint(sketch, "E6.2.8.3", {"position": v(121.92, -432.43) * mm});
            skLineSegment(sketch, "E6.2.8.4", {"start": v(21.27, -553.08) * mm, "end": v(101.92, -553.08) * mm});
            skLineSegment(sketch, "E6.2.8.5", {"start": v(1.27, -452.43) * mm, "end": v(1.27, -533.08) * mm});
            skPoint(sketch, "E6.2.8.6", {"position": v(1.27, -432.43) * mm});
            skLineSegment(sketch, "E6.2.8.7", {"start": v(121.92, -452.43) * mm, "end": v(121.92, -533.08) * mm});
            skArc(sketch, "E6.2.8.8", {"start": v(121.92, -452.43) * mm, "mid": v(116.06, -438.3) * mm, "end": v(101.92, -432.43) * mm});
            skArc(sketch, "E6.2.8.9", {"start": v(101.92, -553.08) * mm, "mid": v(116.06, -547.23) * mm, "end": v(121.92, -533.08) * mm});
            skArc(sketch, "E6.2.8.10", {"start": v(1.27, -533.08) * mm, "mid": v(7.13, -547.23) * mm, "end": v(21.27, -553.08) * mm});
            skArc(sketch, "E6.2.8.11", {"start": v(21.27, -432.43) * mm, "mid": v(7.13, -438.3) * mm, "end": v(1.27, -452.43) * mm});
            skLineSegment(sketch, "E6.3.0.0", {"start": v(144.46, 553.08) * mm, "end": v(225.11, 553.08) * mm});
            skPoint(sketch, "E6.3.0.1", {"position": v(124.46, 432.44) * mm});
            skPoint(sketch, "E6.3.0.2", {"position": v(245.1, 432.44) * mm});
            skPoint(sketch, "E6.3.0.3", {"position": v(245.11, 553.08) * mm});
            skLineSegment(sketch, "E6.3.0.4", {"start": v(144.46, 432.44) * mm, "end": v(225.1, 432.44) * mm});
            skLineSegment(sketch, "E6.3.0.5", {"start": v(124.46, 533.09) * mm, "end": v(124.46, 452.44) * mm});
            skPoint(sketch, "E6.3.0.6", {"position": v(124.46, 553.08) * mm});
            skLineSegment(sketch, "E6.3.0.7", {"start": v(245.11, 533.08) * mm, "end": v(245.11, 452.44) * mm});
            skArc(sketch, "E6.3.0.8", {"start": v(245.1, 533.08) * mm, "mid": v(239.25, 547.23) * mm, "end": v(225.11, 553.08) * mm});
            skArc(sketch, "E6.3.0.9", {"start": v(225.1, 432.43) * mm, "mid": v(239.25, 438.3) * mm, "end": v(245.1, 452.44) * mm});
            skArc(sketch, "E6.3.0.10", {"start": v(124.46, 452.44) * mm, "mid": v(130.32, 438.3) * mm, "end": v(144.46, 432.44) * mm});
            skArc(sketch, "E6.3.0.11", {"start": v(144.46, 553.09) * mm, "mid": v(130.32, 547.23) * mm, "end": v(124.46, 533.09) * mm});
            skLineSegment(sketch, "E6.3.1.0", {"start": v(144.46, 429.9) * mm, "end": v(225.11, 429.9) * mm});
            skPoint(sketch, "E6.3.1.1", {"position": v(124.46, 309.25) * mm});
            skPoint(sketch, "E6.3.1.2", {"position": v(245.1, 309.25) * mm});
            skPoint(sketch, "E6.3.1.3", {"position": v(245.1, 429.9) * mm});
            skLineSegment(sketch, "E6.3.1.4", {"start": v(144.46, 309.25) * mm, "end": v(225.11, 309.25) * mm});
            skLineSegment(sketch, "E6.3.1.5", {"start": v(124.46, 409.9) * mm, "end": v(124.46, 329.25) * mm});
            skPoint(sketch, "E6.3.1.6", {"position": v(124.46, 429.9) * mm});
            skLineSegment(sketch, "E6.3.1.7", {"start": v(245.11, 409.9) * mm, "end": v(245.11, 329.25) * mm});
            skArc(sketch, "E6.3.1.8", {"start": v(245.1, 409.9) * mm, "mid": v(239.25, 424.04) * mm, "end": v(225.11, 429.9) * mm});
            skArc(sketch, "E6.3.1.9", {"start": v(225.11, 309.25) * mm, "mid": v(239.25, 315.1) * mm, "end": v(245.1, 329.25) * mm});
            skArc(sketch, "E6.3.1.10", {"start": v(124.46, 329.25) * mm, "mid": v(130.32, 315.1) * mm, "end": v(144.46, 309.25) * mm});
            skArc(sketch, "E6.3.1.11", {"start": v(144.46, 429.9) * mm, "mid": v(130.32, 424.04) * mm, "end": v(124.46, 409.9) * mm});
            skLineSegment(sketch, "E6.3.2.0", {"start": v(144.46, 306.7) * mm, "end": v(225.11, 306.7) * mm});
            skPoint(sketch, "E6.3.2.1", {"position": v(124.46, 186.06) * mm});
            skPoint(sketch, "E6.3.2.2", {"position": v(245.11, 186.06) * mm});
            skPoint(sketch, "E6.3.2.3", {"position": v(245.11, 306.7) * mm});
            skLineSegment(sketch, "E6.3.2.4", {"start": v(144.46, 186.06) * mm, "end": v(225.11, 186.06) * mm});
            skLineSegment(sketch, "E6.3.2.5", {"start": v(124.46, 286.7) * mm, "end": v(124.46, 206.06) * mm});
            skPoint(sketch, "E6.3.2.6", {"position": v(124.46, 306.7) * mm});
            skLineSegment(sketch, "E6.3.2.7", {"start": v(245.11, 286.7) * mm, "end": v(245.11, 206.06) * mm});
            skArc(sketch, "E6.3.2.8", {"start": v(245.11, 286.7) * mm, "mid": v(239.25, 300.85) * mm, "end": v(225.11, 306.7) * mm});
            skArc(sketch, "E6.3.2.9", {"start": v(225.11, 186.06) * mm, "mid": v(239.25, 191.91) * mm, "end": v(245.11, 206.06) * mm});
            skArc(sketch, "E6.3.2.10", {"start": v(124.46, 206.06) * mm, "mid": v(130.32, 191.91) * mm, "end": v(144.46, 186.06) * mm});
            skArc(sketch, "E6.3.2.11", {"start": v(144.46, 306.7) * mm, "mid": v(130.32, 300.85) * mm, "end": v(124.46, 286.7) * mm});
            skLineSegment(sketch, "E6.3.3.0", {"start": v(144.46, 183.52) * mm, "end": v(225.11, 183.52) * mm});
            skPoint(sketch, "E6.3.3.1", {"position": v(124.46, 62.87) * mm});
            skPoint(sketch, "E6.3.3.2", {"position": v(245.11, 62.87) * mm});
            skPoint(sketch, "E6.3.3.3", {"position": v(245.11, 183.52) * mm});
            skLineSegment(sketch, "E6.3.3.4", {"start": v(144.46, 62.87) * mm, "end": v(225.11, 62.87) * mm});
            skLineSegment(sketch, "E6.3.3.5", {"start": v(124.46, 163.52) * mm, "end": v(124.46, 82.87) * mm});
            skPoint(sketch, "E6.3.3.6", {"position": v(124.46, 183.52) * mm});
            skLineSegment(sketch, "E6.3.3.7", {"start": v(245.11, 163.52) * mm, "end": v(245.11, 82.87) * mm});
            skArc(sketch, "E6.3.3.8", {"start": v(245.11, 163.52) * mm, "mid": v(239.25, 177.66) * mm, "end": v(225.11, 183.52) * mm});
            skArc(sketch, "E6.3.3.9", {"start": v(225.11, 62.87) * mm, "mid": v(239.25, 68.72) * mm, "end": v(245.11, 82.87) * mm});
            skArc(sketch, "E6.3.3.10", {"start": v(124.46, 82.87) * mm, "mid": v(130.32, 68.72) * mm, "end": v(144.46, 62.87) * mm});
            skArc(sketch, "E6.3.3.11", {"start": v(144.46, 183.52) * mm, "mid": v(130.32, 177.66) * mm, "end": v(124.46, 163.52) * mm});
            skLineSegment(sketch, "E6.3.4.0", {"start": v(144.46, 60.33) * mm, "end": v(225.11, 60.33) * mm});
            skPoint(sketch, "E6.3.4.1", {"position": v(124.46, -60.32) * mm});
            skPoint(sketch, "E6.3.4.2", {"position": v(245.11, -60.32) * mm});
            skPoint(sketch, "E6.3.4.3", {"position": v(245.11, 60.33) * mm});
            skLineSegment(sketch, "E6.3.4.4", {"start": v(144.46, -60.32) * mm, "end": v(225.11, -60.32) * mm});
            skLineSegment(sketch, "E6.3.4.5", {"start": v(124.46, 40.33) * mm, "end": v(124.46, -40.32) * mm});
            skPoint(sketch, "E6.3.4.6", {"position": v(124.46, 60.33) * mm});
            skLineSegment(sketch, "E6.3.4.7", {"start": v(245.11, 40.33) * mm, "end": v(245.11, -40.32) * mm});
            skArc(sketch, "E6.3.4.8", {"start": v(245.11, 40.33) * mm, "mid": v(239.25, 54.47) * mm, "end": v(225.11, 60.33) * mm});
            skArc(sketch, "E6.3.4.9", {"start": v(225.11, -60.32) * mm, "mid": v(239.25, -54.47) * mm, "end": v(245.11, -40.32) * mm});
            skArc(sketch, "E6.3.4.10", {"start": v(124.46, -40.32) * mm, "mid": v(130.32, -54.47) * mm, "end": v(144.46, -60.32) * mm});
            skArc(sketch, "E6.3.4.11", {"start": v(144.46, 60.33) * mm, "mid": v(130.32, 54.47) * mm, "end": v(124.46, 40.33) * mm});
            skLineSegment(sketch, "E6.3.5.0", {"start": v(144.46, -62.86) * mm, "end": v(225.11, -62.86) * mm});
            skPoint(sketch, "E6.3.5.1", {"position": v(124.46, -183.51) * mm});
            skPoint(sketch, "E6.3.5.2", {"position": v(245.11, -183.51) * mm});
            skPoint(sketch, "E6.3.5.3", {"position": v(245.11, -62.86) * mm});
            skLineSegment(sketch, "E6.3.5.4", {"start": v(144.46, -183.51) * mm, "end": v(225.11, -183.51) * mm});
            skLineSegment(sketch, "E6.3.5.5", {"start": v(124.46, -82.86) * mm, "end": v(124.46, -163.51) * mm});
            skPoint(sketch, "E6.3.5.6", {"position": v(124.46, -62.86) * mm});
            skLineSegment(sketch, "E6.3.5.7", {"start": v(245.11, -82.86) * mm, "end": v(245.11, -163.51) * mm});
            skArc(sketch, "E6.3.5.8", {"start": v(245.11, -82.86) * mm, "mid": v(239.25, -68.72) * mm, "end": v(225.11, -62.86) * mm});
            skArc(sketch, "E6.3.5.9", {"start": v(225.11, -183.51) * mm, "mid": v(239.25, -177.66) * mm, "end": v(245.11, -163.51) * mm});
            skArc(sketch, "E6.3.5.10", {"start": v(124.46, -163.51) * mm, "mid": v(130.32, -177.66) * mm, "end": v(144.46, -183.51) * mm});
            skArc(sketch, "E6.3.5.11", {"start": v(144.46, -62.86) * mm, "mid": v(130.32, -68.72) * mm, "end": v(124.46, -82.86) * mm});
            skLineSegment(sketch, "E6.3.6.0", {"start": v(144.46, -186.05) * mm, "end": v(225.11, -186.05) * mm});
            skPoint(sketch, "E6.3.6.1", {"position": v(124.46, -306.7) * mm});
            skPoint(sketch, "E6.3.6.2", {"position": v(245.11, -306.7) * mm});
            skPoint(sketch, "E6.3.6.3", {"position": v(245.11, -186.05) * mm});
            skLineSegment(sketch, "E6.3.6.4", {"start": v(144.46, -306.7) * mm, "end": v(225.11, -306.7) * mm});
            skLineSegment(sketch, "E6.3.6.5", {"start": v(124.46, -206.05) * mm, "end": v(124.46, -286.7) * mm});
            skPoint(sketch, "E6.3.6.6", {"position": v(124.46, -186.05) * mm});
            skLineSegment(sketch, "E6.3.6.7", {"start": v(245.11, -206.05) * mm, "end": v(245.11, -286.7) * mm});
            skArc(sketch, "E6.3.6.8", {"start": v(245.11, -206.05) * mm, "mid": v(239.25, -191.91) * mm, "end": v(225.11, -186.05) * mm});
            skArc(sketch, "E6.3.6.9", {"start": v(225.11, -306.7) * mm, "mid": v(239.25, -300.85) * mm, "end": v(245.11, -286.7) * mm});
            skArc(sketch, "E6.3.6.10", {"start": v(124.46, -286.7) * mm, "mid": v(130.32, -300.85) * mm, "end": v(144.46, -306.7) * mm});
            skArc(sketch, "E6.3.6.11", {"start": v(144.46, -186.05) * mm, "mid": v(130.32, -191.91) * mm, "end": v(124.46, -206.05) * mm});
            skLineSegment(sketch, "E6.3.7.0", {"start": v(144.46, -309.24) * mm, "end": v(225.11, -309.24) * mm});
            skPoint(sketch, "E6.3.7.1", {"position": v(124.46, -429.9) * mm});
            skPoint(sketch, "E6.3.7.2", {"position": v(245.11, -429.9) * mm});
            skPoint(sketch, "E6.3.7.3", {"position": v(245.11, -309.24) * mm});
            skLineSegment(sketch, "E6.3.7.4", {"start": v(144.46, -429.9) * mm, "end": v(225.11, -429.9) * mm});
            skLineSegment(sketch, "E6.3.7.5", {"start": v(124.46, -329.24) * mm, "end": v(124.46, -409.9) * mm});
            skPoint(sketch, "E6.3.7.6", {"position": v(124.46, -309.24) * mm});
            skLineSegment(sketch, "E6.3.7.7", {"start": v(245.11, -329.24) * mm, "end": v(245.11, -409.9) * mm});
            skArc(sketch, "E6.3.7.8", {"start": v(245.11, -329.24) * mm, "mid": v(239.25, -315.1) * mm, "end": v(225.11, -309.24) * mm});
            skArc(sketch, "E6.3.7.9", {"start": v(225.11, -429.9) * mm, "mid": v(239.25, -424.04) * mm, "end": v(245.11, -409.9) * mm});
            skArc(sketch, "E6.3.7.10", {"start": v(124.46, -409.9) * mm, "mid": v(130.32, -424.04) * mm, "end": v(144.46, -429.9) * mm});
            skArc(sketch, "E6.3.7.11", {"start": v(144.46, -309.24) * mm, "mid": v(130.32, -315.1) * mm, "end": v(124.46, -329.24) * mm});
            skLineSegment(sketch, "E6.3.8.0", {"start": v(144.46, -432.43) * mm, "end": v(225.11, -432.43) * mm});
            skPoint(sketch, "E6.3.8.1", {"position": v(124.46, -553.08) * mm});
            skPoint(sketch, "E6.3.8.2", {"position": v(245.11, -553.08) * mm});
            skPoint(sketch, "E6.3.8.3", {"position": v(245.11, -432.43) * mm});
            skLineSegment(sketch, "E6.3.8.4", {"start": v(144.46, -553.08) * mm, "end": v(225.11, -553.08) * mm});
            skLineSegment(sketch, "E6.3.8.5", {"start": v(124.46, -452.43) * mm, "end": v(124.46, -533.08) * mm});
            skPoint(sketch, "E6.3.8.6", {"position": v(124.46, -432.43) * mm});
            skLineSegment(sketch, "E6.3.8.7", {"start": v(245.11, -452.43) * mm, "end": v(245.11, -533.08) * mm});
            skArc(sketch, "E6.3.8.8", {"start": v(245.11, -452.43) * mm, "mid": v(239.25, -438.3) * mm, "end": v(225.11, -432.43) * mm});
            skArc(sketch, "E6.3.8.9", {"start": v(225.11, -553.08) * mm, "mid": v(239.25, -547.23) * mm, "end": v(245.11, -533.08) * mm});
            skArc(sketch, "E6.3.8.10", {"start": v(124.46, -533.08) * mm, "mid": v(130.32, -547.23) * mm, "end": v(144.46, -553.08) * mm});
            skArc(sketch, "E6.3.8.11", {"start": v(144.46, -432.43) * mm, "mid": v(130.32, -438.3) * mm, "end": v(124.46, -452.43) * mm});
            skLineSegment(sketch, "E6.direction1", {"start": v(-225.1, 553.09) * mm, "end": v(-101.92, 553.09) * mm, "construction": true});
            skLineSegment(sketch, "E6.direction2", {"start": v(-225.1, 553.09) * mm, "end": v(-225.1, 429.9) * mm, "construction": true});
            skSolve(sketch);
        }
        {
            var Q0;
            Q0 = qSketchRegion(id + "F2", true);
            var Q1;
            Q1=makeQuery(id+"F1.opExtrude","CAP_FACE",FACE,{"disambiguationData":[OSD([sQuery(id+"F0.wireOp",EDGE,"E0.bottom"),sQuery(id+"F0.wireOp",EDGE,"E0.top"),sQuery(id+"F0.wireOp",EDGE,"E0.left"),sQuery(id+"F0.wireOp",EDGE,"E0.right")])],"isStart":false});
            var Q2;
            Q2=makeQuery(id+"F1.opExtrude","CAP_FACE",FACE,{"disambiguationData":[OSD([sQuery(id+"F0.wireOp",EDGE,"E0.bottom"),sQuery(id+"F0.wireOp",EDGE,"E0.top"),sQuery(id+"F0.wireOp",EDGE,"E0.left"),sQuery(id+"F0.wireOp",EDGE,"E0.right")])],"isStart":false});
            extrude(context, id + "F3", {"entities" : qUnion([Q0]), "operationType" : NewBodyOperationType.REMOVE, "endBound" : BoundingType.UP_TO_SURFACE, "depth" : 36.5 * mm, "endBoundEntityFace" : qUnion([Q1]), "offsetDistance" : 1.59 * mm, "offsetOppositeDirection" : true, "hasSecondDirection" : true, "secondDirectionOppositeDirection" : false, "secondDirectionDepth" : 36.5 * mm, "secondDirectionBoundEntityFace" : qUnion([Q2])});
        }
        {
            var Q0;
            Q0=makeQuery(id+"F3.boolean.opBoolean","COPY",FACE,{"derivedFrom":makeQuery(id+"F3.opExtrude","CAP_FACE",FACE,{"disambiguationData":[OSD([sQuery(id+"F2.wireOp",EDGE,"E6.0.8.0"),sQuery(id+"F2.wireOp",EDGE,"E6.0.8.4"),sQuery(id+"F2.wireOp",EDGE,"E6.0.8.5"),sQuery(id+"F2.wireOp",EDGE,"E6.0.8.7"),sQuery(id+"F2.wireOp",EDGE,"E6.0.8.8"),sQuery(id+"F2.wireOp",EDGE,"E6.0.8.9"),sQuery(id+"F2.wireOp",EDGE,"E6.0.8.10"),sQuery(id+"F2.wireOp",EDGE,"E6.0.8.11")])],"isStart":true})});
            var Q1;
            Q1=makeQuery(id+"F3.boolean.opBoolean","COPY",FACE,{"derivedFrom":makeQuery(id+"F3.opExtrude","CAP_FACE",FACE,{"disambiguationData":[OSD([sQuery(id+"F2.wireOp",EDGE,"E6.1.8.0"),sQuery(id+"F2.wireOp",EDGE,"E6.1.8.4"),sQuery(id+"F2.wireOp",EDGE,"E6.1.8.5"),sQuery(id+"F2.wireOp",EDGE,"E6.1.8.7"),sQuery(id+"F2.wireOp",EDGE,"E6.1.8.8"),sQuery(id+"F2.wireOp",EDGE,"E6.1.8.9"),sQuery(id+"F2.wireOp",EDGE,"E6.1.8.10"),sQuery(id+"F2.wireOp",EDGE,"E6.1.8.11")])],"isStart":true})});
            var Q2;
            Q2=makeQuery(id+"F3.boolean.opBoolean","COPY",FACE,{"derivedFrom":makeQuery(id+"F3.opExtrude","CAP_FACE",FACE,{"disambiguationData":[OSD([sQuery(id+"F2.wireOp",EDGE,"E6.2.8.0"),sQuery(id+"F2.wireOp",EDGE,"E6.2.8.4"),sQuery(id+"F2.wireOp",EDGE,"E6.2.8.5"),sQuery(id+"F2.wireOp",EDGE,"E6.2.8.7"),sQuery(id+"F2.wireOp",EDGE,"E6.2.8.8"),sQuery(id+"F2.wireOp",EDGE,"E6.2.8.9"),sQuery(id+"F2.wireOp",EDGE,"E6.2.8.10"),sQuery(id+"F2.wireOp",EDGE,"E6.2.8.11")])],"isStart":true})});
            var Q3;
            Q3=makeQuery(id+"F3.boolean.opBoolean","COPY",FACE,{"derivedFrom":makeQuery(id+"F3.opExtrude","CAP_FACE",FACE,{"disambiguationData":[OSD([sQuery(id+"F2.wireOp",EDGE,"E6.3.8.0"),sQuery(id+"F2.wireOp",EDGE,"E6.3.8.4"),sQuery(id+"F2.wireOp",EDGE,"E6.3.8.5"),sQuery(id+"F2.wireOp",EDGE,"E6.3.8.7"),sQuery(id+"F2.wireOp",EDGE,"E6.3.8.8"),sQuery(id+"F2.wireOp",EDGE,"E6.3.8.9"),sQuery(id+"F2.wireOp",EDGE,"E6.3.8.10"),sQuery(id+"F2.wireOp",EDGE,"E6.3.8.11")])],"isStart":true})});
            var Q4;
            Q4=makeQuery(id+"F3.boolean.opBoolean","COPY",FACE,{"derivedFrom":makeQuery(id+"F3.opExtrude","CAP_FACE",FACE,{"disambiguationData":[OSD([sQuery(id+"F2.wireOp",EDGE,"E6.3.7.0"),sQuery(id+"F2.wireOp",EDGE,"E6.3.7.4"),sQuery(id+"F2.wireOp",EDGE,"E6.3.7.5"),sQuery(id+"F2.wireOp",EDGE,"E6.3.7.7"),sQuery(id+"F2.wireOp",EDGE,"E6.3.7.8"),sQuery(id+"F2.wireOp",EDGE,"E6.3.7.9"),sQuery(id+"F2.wireOp",EDGE,"E6.3.7.10"),sQuery(id+"F2.wireOp",EDGE,"E6.3.7.11")])],"isStart":true})});
            var Q5;
            Q5=makeQuery(id+"F3.boolean.opBoolean","COPY",FACE,{"derivedFrom":makeQuery(id+"F3.opExtrude","CAP_FACE",FACE,{"disambiguationData":[OSD([sQuery(id+"F2.wireOp",EDGE,"E6.2.7.0"),sQuery(id+"F2.wireOp",EDGE,"E6.2.7.4"),sQuery(id+"F2.wireOp",EDGE,"E6.2.7.5"),sQuery(id+"F2.wireOp",EDGE,"E6.2.7.7"),sQuery(id+"F2.wireOp",EDGE,"E6.2.7.8"),sQuery(id+"F2.wireOp",EDGE,"E6.2.7.9"),sQuery(id+"F2.wireOp",EDGE,"E6.2.7.10"),sQuery(id+"F2.wireOp",EDGE,"E6.2.7.11")])],"isStart":true})});
            var Q6;
            Q6=makeQuery(id+"F3.boolean.opBoolean","COPY",FACE,{"derivedFrom":makeQuery(id+"F3.opExtrude","CAP_FACE",FACE,{"disambiguationData":[OSD([sQuery(id+"F2.wireOp",EDGE,"E6.1.7.0"),sQuery(id+"F2.wireOp",EDGE,"E6.1.7.4"),sQuery(id+"F2.wireOp",EDGE,"E6.1.7.5"),sQuery(id+"F2.wireOp",EDGE,"E6.1.7.7"),sQuery(id+"F2.wireOp",EDGE,"E6.1.7.8"),sQuery(id+"F2.wireOp",EDGE,"E6.1.7.9"),sQuery(id+"F2.wireOp",EDGE,"E6.1.7.10"),sQuery(id+"F2.wireOp",EDGE,"E6.1.7.11")])],"isStart":true})});
            var Q7;
            Q7=makeQuery(id+"F3.boolean.opBoolean","COPY",FACE,{"derivedFrom":makeQuery(id+"F3.opExtrude","CAP_FACE",FACE,{"disambiguationData":[OSD([sQuery(id+"F2.wireOp",EDGE,"E6.0.7.0"),sQuery(id+"F2.wireOp",EDGE,"E6.0.7.4"),sQuery(id+"F2.wireOp",EDGE,"E6.0.7.5"),sQuery(id+"F2.wireOp",EDGE,"E6.0.7.7"),sQuery(id+"F2.wireOp",EDGE,"E6.0.7.8"),sQuery(id+"F2.wireOp",EDGE,"E6.0.7.9"),sQuery(id+"F2.wireOp",EDGE,"E6.0.7.10"),sQuery(id+"F2.wireOp",EDGE,"E6.0.7.11")])],"isStart":true})});
            var Q8;
            Q8=makeQuery(id+"F3.boolean.opBoolean","COPY",FACE,{"derivedFrom":makeQuery(id+"F3.opExtrude","CAP_FACE",FACE,{"disambiguationData":[OSD([sQuery(id+"F2.wireOp",EDGE,"E6.0.6.0"),sQuery(id+"F2.wireOp",EDGE,"E6.0.6.4"),sQuery(id+"F2.wireOp",EDGE,"E6.0.6.5"),sQuery(id+"F2.wireOp",EDGE,"E6.0.6.7"),sQuery(id+"F2.wireOp",EDGE,"E6.0.6.8"),sQuery(id+"F2.wireOp",EDGE,"E6.0.6.9"),sQuery(id+"F2.wireOp",EDGE,"E6.0.6.10"),sQuery(id+"F2.wireOp",EDGE,"E6.0.6.11")])],"isStart":true})});
            var Q9;
            Q9=makeQuery(id+"F3.boolean.opBoolean","COPY",FACE,{"derivedFrom":makeQuery(id+"F3.opExtrude","CAP_FACE",FACE,{"disambiguationData":[OSD([sQuery(id+"F2.wireOp",EDGE,"E6.1.6.0"),sQuery(id+"F2.wireOp",EDGE,"E6.1.6.4"),sQuery(id+"F2.wireOp",EDGE,"E6.1.6.5"),sQuery(id+"F2.wireOp",EDGE,"E6.1.6.7"),sQuery(id+"F2.wireOp",EDGE,"E6.1.6.8"),sQuery(id+"F2.wireOp",EDGE,"E6.1.6.9"),sQuery(id+"F2.wireOp",EDGE,"E6.1.6.10"),sQuery(id+"F2.wireOp",EDGE,"E6.1.6.11")])],"isStart":true})});
            var Q10;
            Q10=makeQuery(id+"F3.boolean.opBoolean","COPY",FACE,{"derivedFrom":makeQuery(id+"F3.opExtrude","CAP_FACE",FACE,{"disambiguationData":[OSD([sQuery(id+"F2.wireOp",EDGE,"E6.2.6.0"),sQuery(id+"F2.wireOp",EDGE,"E6.2.6.4"),sQuery(id+"F2.wireOp",EDGE,"E6.2.6.5"),sQuery(id+"F2.wireOp",EDGE,"E6.2.6.7"),sQuery(id+"F2.wireOp",EDGE,"E6.2.6.8"),sQuery(id+"F2.wireOp",EDGE,"E6.2.6.9"),sQuery(id+"F2.wireOp",EDGE,"E6.2.6.10"),sQuery(id+"F2.wireOp",EDGE,"E6.2.6.11")])],"isStart":true})});
            var Q11;
            Q11=makeQuery(id+"F3.boolean.opBoolean","COPY",FACE,{"derivedFrom":makeQuery(id+"F3.opExtrude","CAP_FACE",FACE,{"disambiguationData":[OSD([sQuery(id+"F2.wireOp",EDGE,"E6.3.6.0"),sQuery(id+"F2.wireOp",EDGE,"E6.3.6.4"),sQuery(id+"F2.wireOp",EDGE,"E6.3.6.5"),sQuery(id+"F2.wireOp",EDGE,"E6.3.6.7"),sQuery(id+"F2.wireOp",EDGE,"E6.3.6.8"),sQuery(id+"F2.wireOp",EDGE,"E6.3.6.9"),sQuery(id+"F2.wireOp",EDGE,"E6.3.6.10"),sQuery(id+"F2.wireOp",EDGE,"E6.3.6.11")])],"isStart":true})});
            var Q12;
            Q12=makeQuery(id+"F3.boolean.opBoolean","COPY",FACE,{"derivedFrom":makeQuery(id+"F3.opExtrude","CAP_FACE",FACE,{"disambiguationData":[OSD([sQuery(id+"F2.wireOp",EDGE,"E6.3.5.0"),sQuery(id+"F2.wireOp",EDGE,"E6.3.5.4"),sQuery(id+"F2.wireOp",EDGE,"E6.3.5.5"),sQuery(id+"F2.wireOp",EDGE,"E6.3.5.7"),sQuery(id+"F2.wireOp",EDGE,"E6.3.5.8"),sQuery(id+"F2.wireOp",EDGE,"E6.3.5.9"),sQuery(id+"F2.wireOp",EDGE,"E6.3.5.10"),sQuery(id+"F2.wireOp",EDGE,"E6.3.5.11")])],"isStart":true})});
            var Q13;
            Q13=makeQuery(id+"F3.boolean.opBoolean","COPY",FACE,{"derivedFrom":makeQuery(id+"F3.opExtrude","CAP_FACE",FACE,{"disambiguationData":[OSD([sQuery(id+"F2.wireOp",EDGE,"E6.2.5.0"),sQuery(id+"F2.wireOp",EDGE,"E6.2.5.4"),sQuery(id+"F2.wireOp",EDGE,"E6.2.5.5"),sQuery(id+"F2.wireOp",EDGE,"E6.2.5.7"),sQuery(id+"F2.wireOp",EDGE,"E6.2.5.8"),sQuery(id+"F2.wireOp",EDGE,"E6.2.5.9"),sQuery(id+"F2.wireOp",EDGE,"E6.2.5.10"),sQuery(id+"F2.wireOp",EDGE,"E6.2.5.11")])],"isStart":true})});
            var Q14;
            Q14=makeQuery(id+"F3.boolean.opBoolean","COPY",FACE,{"derivedFrom":makeQuery(id+"F3.opExtrude","CAP_FACE",FACE,{"disambiguationData":[OSD([sQuery(id+"F2.wireOp",EDGE,"E6.1.5.0"),sQuery(id+"F2.wireOp",EDGE,"E6.1.5.4"),sQuery(id+"F2.wireOp",EDGE,"E6.1.5.5"),sQuery(id+"F2.wireOp",EDGE,"E6.1.5.7"),sQuery(id+"F2.wireOp",EDGE,"E6.1.5.8"),sQuery(id+"F2.wireOp",EDGE,"E6.1.5.9"),sQuery(id+"F2.wireOp",EDGE,"E6.1.5.10"),sQuery(id+"F2.wireOp",EDGE,"E6.1.5.11")])],"isStart":true})});
            var Q15;
            Q15=makeQuery(id+"F3.boolean.opBoolean","COPY",FACE,{"derivedFrom":makeQuery(id+"F3.opExtrude","CAP_FACE",FACE,{"disambiguationData":[OSD([sQuery(id+"F2.wireOp",EDGE,"E6.0.5.0"),sQuery(id+"F2.wireOp",EDGE,"E6.0.5.4"),sQuery(id+"F2.wireOp",EDGE,"E6.0.5.5"),sQuery(id+"F2.wireOp",EDGE,"E6.0.5.7"),sQuery(id+"F2.wireOp",EDGE,"E6.0.5.8"),sQuery(id+"F2.wireOp",EDGE,"E6.0.5.9"),sQuery(id+"F2.wireOp",EDGE,"E6.0.5.10"),sQuery(id+"F2.wireOp",EDGE,"E6.0.5.11")])],"isStart":true})});
            var Q16;
            Q16=makeQuery(id+"F3.boolean.opBoolean","COPY",FACE,{"derivedFrom":makeQuery(id+"F3.opExtrude","CAP_FACE",FACE,{"disambiguationData":[OSD([sQuery(id+"F2.wireOp",EDGE,"E6.0.4.0"),sQuery(id+"F2.wireOp",EDGE,"E6.0.4.4"),sQuery(id+"F2.wireOp",EDGE,"E6.0.4.5"),sQuery(id+"F2.wireOp",EDGE,"E6.0.4.7"),sQuery(id+"F2.wireOp",EDGE,"E6.0.4.8"),sQuery(id+"F2.wireOp",EDGE,"E6.0.4.9"),sQuery(id+"F2.wireOp",EDGE,"E6.0.4.10"),sQuery(id+"F2.wireOp",EDGE,"E6.0.4.11")])],"isStart":true})});
            var Q17;
            Q17=makeQuery(id+"F3.boolean.opBoolean","COPY",FACE,{"derivedFrom":makeQuery(id+"F3.opExtrude","CAP_FACE",FACE,{"disambiguationData":[OSD([sQuery(id+"F2.wireOp",EDGE,"E6.1.4.0"),sQuery(id+"F2.wireOp",EDGE,"E6.1.4.4"),sQuery(id+"F2.wireOp",EDGE,"E6.1.4.5"),sQuery(id+"F2.wireOp",EDGE,"E6.1.4.7"),sQuery(id+"F2.wireOp",EDGE,"E6.1.4.8"),sQuery(id+"F2.wireOp",EDGE,"E6.1.4.9"),sQuery(id+"F2.wireOp",EDGE,"E6.1.4.10"),sQuery(id+"F2.wireOp",EDGE,"E6.1.4.11")])],"isStart":true})});
            var Q18;
            Q18=makeQuery(id+"F3.boolean.opBoolean","COPY",FACE,{"derivedFrom":makeQuery(id+"F3.opExtrude","CAP_FACE",FACE,{"disambiguationData":[OSD([sQuery(id+"F2.wireOp",EDGE,"E6.2.4.0"),sQuery(id+"F2.wireOp",EDGE,"E6.2.4.4"),sQuery(id+"F2.wireOp",EDGE,"E6.2.4.5"),sQuery(id+"F2.wireOp",EDGE,"E6.2.4.7"),sQuery(id+"F2.wireOp",EDGE,"E6.2.4.8"),sQuery(id+"F2.wireOp",EDGE,"E6.2.4.9"),sQuery(id+"F2.wireOp",EDGE,"E6.2.4.10"),sQuery(id+"F2.wireOp",EDGE,"E6.2.4.11")])],"isStart":true})});
            var Q19;
            Q19=makeQuery(id+"F3.boolean.opBoolean","COPY",FACE,{"derivedFrom":makeQuery(id+"F3.opExtrude","CAP_FACE",FACE,{"disambiguationData":[OSD([sQuery(id+"F2.wireOp",EDGE,"E6.3.4.0"),sQuery(id+"F2.wireOp",EDGE,"E6.3.4.4"),sQuery(id+"F2.wireOp",EDGE,"E6.3.4.5"),sQuery(id+"F2.wireOp",EDGE,"E6.3.4.7"),sQuery(id+"F2.wireOp",EDGE,"E6.3.4.8"),sQuery(id+"F2.wireOp",EDGE,"E6.3.4.9"),sQuery(id+"F2.wireOp",EDGE,"E6.3.4.10"),sQuery(id+"F2.wireOp",EDGE,"E6.3.4.11")])],"isStart":true})});
            var Q20;
            Q20=makeQuery(id+"F3.boolean.opBoolean","COPY",FACE,{"derivedFrom":makeQuery(id+"F3.opExtrude","CAP_FACE",FACE,{"disambiguationData":[OSD([sQuery(id+"F2.wireOp",EDGE,"E6.3.3.0"),sQuery(id+"F2.wireOp",EDGE,"E6.3.3.4"),sQuery(id+"F2.wireOp",EDGE,"E6.3.3.5"),sQuery(id+"F2.wireOp",EDGE,"E6.3.3.7"),sQuery(id+"F2.wireOp",EDGE,"E6.3.3.8"),sQuery(id+"F2.wireOp",EDGE,"E6.3.3.9"),sQuery(id+"F2.wireOp",EDGE,"E6.3.3.10"),sQuery(id+"F2.wireOp",EDGE,"E6.3.3.11")])],"isStart":true})});
            var Q21;
            Q21=makeQuery(id+"F3.boolean.opBoolean","COPY",FACE,{"derivedFrom":makeQuery(id+"F3.opExtrude","CAP_FACE",FACE,{"disambiguationData":[OSD([sQuery(id+"F2.wireOp",EDGE,"E6.2.3.0"),sQuery(id+"F2.wireOp",EDGE,"E6.2.3.4"),sQuery(id+"F2.wireOp",EDGE,"E6.2.3.5"),sQuery(id+"F2.wireOp",EDGE,"E6.2.3.7"),sQuery(id+"F2.wireOp",EDGE,"E6.2.3.8"),sQuery(id+"F2.wireOp",EDGE,"E6.2.3.9"),sQuery(id+"F2.wireOp",EDGE,"E6.2.3.10"),sQuery(id+"F2.wireOp",EDGE,"E6.2.3.11")])],"isStart":true})});
            var Q22;
            Q22=makeQuery(id+"F3.boolean.opBoolean","COPY",FACE,{"derivedFrom":makeQuery(id+"F3.opExtrude","CAP_FACE",FACE,{"disambiguationData":[OSD([sQuery(id+"F2.wireOp",EDGE,"E6.1.3.0"),sQuery(id+"F2.wireOp",EDGE,"E6.1.3.4"),sQuery(id+"F2.wireOp",EDGE,"E6.1.3.5"),sQuery(id+"F2.wireOp",EDGE,"E6.1.3.7"),sQuery(id+"F2.wireOp",EDGE,"E6.1.3.8"),sQuery(id+"F2.wireOp",EDGE,"E6.1.3.9"),sQuery(id+"F2.wireOp",EDGE,"E6.1.3.10"),sQuery(id+"F2.wireOp",EDGE,"E6.1.3.11")])],"isStart":true})});
            var Q23;
            Q23=makeQuery(id+"F3.boolean.opBoolean","COPY",FACE,{"derivedFrom":makeQuery(id+"F3.opExtrude","CAP_FACE",FACE,{"disambiguationData":[OSD([sQuery(id+"F2.wireOp",EDGE,"E6.0.3.0"),sQuery(id+"F2.wireOp",EDGE,"E6.0.3.4"),sQuery(id+"F2.wireOp",EDGE,"E6.0.3.5"),sQuery(id+"F2.wireOp",EDGE,"E6.0.3.7"),sQuery(id+"F2.wireOp",EDGE,"E6.0.3.8"),sQuery(id+"F2.wireOp",EDGE,"E6.0.3.9"),sQuery(id+"F2.wireOp",EDGE,"E6.0.3.10"),sQuery(id+"F2.wireOp",EDGE,"E6.0.3.11")])],"isStart":true})});
            var Q24;
            Q24=makeQuery(id+"F3.boolean.opBoolean","COPY",FACE,{"derivedFrom":makeQuery(id+"F3.opExtrude","CAP_FACE",FACE,{"disambiguationData":[OSD([sQuery(id+"F2.wireOp",EDGE,"E6.0.2.0"),sQuery(id+"F2.wireOp",EDGE,"E6.0.2.4"),sQuery(id+"F2.wireOp",EDGE,"E6.0.2.5"),sQuery(id+"F2.wireOp",EDGE,"E6.0.2.7"),sQuery(id+"F2.wireOp",EDGE,"E6.0.2.8"),sQuery(id+"F2.wireOp",EDGE,"E6.0.2.9"),sQuery(id+"F2.wireOp",EDGE,"E6.0.2.10"),sQuery(id+"F2.wireOp",EDGE,"E6.0.2.11")])],"isStart":true})});
            var Q25;
            Q25=makeQuery(id+"F3.boolean.opBoolean","COPY",FACE,{"derivedFrom":makeQuery(id+"F3.opExtrude","CAP_FACE",FACE,{"disambiguationData":[OSD([sQuery(id+"F2.wireOp",EDGE,"E6.1.2.0"),sQuery(id+"F2.wireOp",EDGE,"E6.1.2.4"),sQuery(id+"F2.wireOp",EDGE,"E6.1.2.5"),sQuery(id+"F2.wireOp",EDGE,"E6.1.2.7"),sQuery(id+"F2.wireOp",EDGE,"E6.1.2.8"),sQuery(id+"F2.wireOp",EDGE,"E6.1.2.9"),sQuery(id+"F2.wireOp",EDGE,"E6.1.2.10"),sQuery(id+"F2.wireOp",EDGE,"E6.1.2.11")])],"isStart":true})});
            var Q26;
            Q26=makeQuery(id+"F3.boolean.opBoolean","COPY",FACE,{"derivedFrom":makeQuery(id+"F3.opExtrude","CAP_FACE",FACE,{"disambiguationData":[OSD([sQuery(id+"F2.wireOp",EDGE,"E6.2.2.0"),sQuery(id+"F2.wireOp",EDGE,"E6.2.2.4"),sQuery(id+"F2.wireOp",EDGE,"E6.2.2.5"),sQuery(id+"F2.wireOp",EDGE,"E6.2.2.7"),sQuery(id+"F2.wireOp",EDGE,"E6.2.2.8"),sQuery(id+"F2.wireOp",EDGE,"E6.2.2.9"),sQuery(id+"F2.wireOp",EDGE,"E6.2.2.10"),sQuery(id+"F2.wireOp",EDGE,"E6.2.2.11")])],"isStart":true})});
            var Q27;
            Q27=makeQuery(id+"F3.boolean.opBoolean","COPY",FACE,{"derivedFrom":makeQuery(id+"F3.opExtrude","CAP_FACE",FACE,{"disambiguationData":[OSD([sQuery(id+"F2.wireOp",EDGE,"E6.3.2.0"),sQuery(id+"F2.wireOp",EDGE,"E6.3.2.4"),sQuery(id+"F2.wireOp",EDGE,"E6.3.2.5"),sQuery(id+"F2.wireOp",EDGE,"E6.3.2.7"),sQuery(id+"F2.wireOp",EDGE,"E6.3.2.8"),sQuery(id+"F2.wireOp",EDGE,"E6.3.2.9"),sQuery(id+"F2.wireOp",EDGE,"E6.3.2.10"),sQuery(id+"F2.wireOp",EDGE,"E6.3.2.11")])],"isStart":true})});
            var Q28;
            Q28=makeQuery(id+"F3.boolean.opBoolean","COPY",FACE,{"derivedFrom":makeQuery(id+"F3.opExtrude","CAP_FACE",FACE,{"disambiguationData":[OSD([sQuery(id+"F2.wireOp",EDGE,"E6.3.1.0"),sQuery(id+"F2.wireOp",EDGE,"E6.3.1.4"),sQuery(id+"F2.wireOp",EDGE,"E6.3.1.5"),sQuery(id+"F2.wireOp",EDGE,"E6.3.1.7"),sQuery(id+"F2.wireOp",EDGE,"E6.3.1.8"),sQuery(id+"F2.wireOp",EDGE,"E6.3.1.9"),sQuery(id+"F2.wireOp",EDGE,"E6.3.1.10"),sQuery(id+"F2.wireOp",EDGE,"E6.3.1.11")])],"isStart":true})});
            var Q29;
            Q29=makeQuery(id+"F3.boolean.opBoolean","COPY",FACE,{"derivedFrom":makeQuery(id+"F3.opExtrude","CAP_FACE",FACE,{"disambiguationData":[OSD([sQuery(id+"F2.wireOp",EDGE,"E6.2.1.0"),sQuery(id+"F2.wireOp",EDGE,"E6.2.1.4"),sQuery(id+"F2.wireOp",EDGE,"E6.2.1.5"),sQuery(id+"F2.wireOp",EDGE,"E6.2.1.7"),sQuery(id+"F2.wireOp",EDGE,"E6.2.1.8"),sQuery(id+"F2.wireOp",EDGE,"E6.2.1.9"),sQuery(id+"F2.wireOp",EDGE,"E6.2.1.10"),sQuery(id+"F2.wireOp",EDGE,"E6.2.1.11")])],"isStart":true})});
            var Q30;
            Q30=makeQuery(id+"F3.boolean.opBoolean","COPY",FACE,{"derivedFrom":makeQuery(id+"F3.opExtrude","CAP_FACE",FACE,{"disambiguationData":[OSD([sQuery(id+"F2.wireOp",EDGE,"E6.1.1.0"),sQuery(id+"F2.wireOp",EDGE,"E6.1.1.4"),sQuery(id+"F2.wireOp",EDGE,"E6.1.1.5"),sQuery(id+"F2.wireOp",EDGE,"E6.1.1.7"),sQuery(id+"F2.wireOp",EDGE,"E6.1.1.8"),sQuery(id+"F2.wireOp",EDGE,"E6.1.1.9"),sQuery(id+"F2.wireOp",EDGE,"E6.1.1.10"),sQuery(id+"F2.wireOp",EDGE,"E6.1.1.11")])],"isStart":true})});
            var Q31;
            Q31=makeQuery(id+"F3.boolean.opBoolean","COPY",FACE,{"derivedFrom":makeQuery(id+"F3.opExtrude","CAP_FACE",FACE,{"disambiguationData":[OSD([sQuery(id+"F2.wireOp",EDGE,"E6.0.1.0"),sQuery(id+"F2.wireOp",EDGE,"E6.0.1.4"),sQuery(id+"F2.wireOp",EDGE,"E6.0.1.5"),sQuery(id+"F2.wireOp",EDGE,"E6.0.1.7"),sQuery(id+"F2.wireOp",EDGE,"E6.0.1.8"),sQuery(id+"F2.wireOp",EDGE,"E6.0.1.9"),sQuery(id+"F2.wireOp",EDGE,"E6.0.1.10"),sQuery(id+"F2.wireOp",EDGE,"E6.0.1.11")])],"isStart":true})});
            var Q32;
            Q32=makeQuery(id+"F3.boolean.opBoolean","COPY",FACE,{"derivedFrom":makeQuery(id+"F3.opExtrude","CAP_FACE",FACE,{"disambiguationData":[OSD([sQuery(id+"F2.wireOp",EDGE,"E6.0.2.0"),sQuery(id+"F2.wireOp",EDGE,"E6.0.2.4"),sQuery(id+"F2.wireOp",EDGE,"E6.0.2.5"),sQuery(id+"F2.wireOp",EDGE,"E6.0.2.7"),sQuery(id+"F2.wireOp",EDGE,"E6.0.2.8"),sQuery(id+"F2.wireOp",EDGE,"E6.0.2.9"),sQuery(id+"F2.wireOp",EDGE,"E6.0.2.10"),sQuery(id+"F2.wireOp",EDGE,"E6.0.2.11")])],"isStart":true})});
            var Q33;
            Q33=makeQuery(id+"F3.boolean.opBoolean","COPY",FACE,{"derivedFrom":makeQuery(id+"F3.opExtrude","CAP_FACE",FACE,{"disambiguationData":[OSD([sQuery(id+"F2.wireOp",EDGE,"E1.bottom"),sQuery(id+"F2.wireOp",EDGE,"E1.top"),sQuery(id+"F2.wireOp",EDGE,"E1.left"),sQuery(id+"F2.wireOp",EDGE,"E1.right"),sQuery(id+"F2.wireOp",EDGE,"E2.filletArc"),sQuery(id+"F2.wireOp",EDGE,"E3.filletArc"),sQuery(id+"F2.wireOp",EDGE,"E4.filletArc"),sQuery(id+"F2.wireOp",EDGE,"E5.filletArc")])],"isStart":true})});
            var Q34;
            Q34=makeQuery(id+"F3.boolean.opBoolean","COPY",FACE,{"derivedFrom":makeQuery(id+"F3.opExtrude","CAP_FACE",FACE,{"disambiguationData":[OSD([sQuery(id+"F2.wireOp",EDGE,"E6.1.0.0"),sQuery(id+"F2.wireOp",EDGE,"E6.1.0.4"),sQuery(id+"F2.wireOp",EDGE,"E6.1.0.5"),sQuery(id+"F2.wireOp",EDGE,"E6.1.0.7"),sQuery(id+"F2.wireOp",EDGE,"E6.1.0.8"),sQuery(id+"F2.wireOp",EDGE,"E6.1.0.9"),sQuery(id+"F2.wireOp",EDGE,"E6.1.0.10"),sQuery(id+"F2.wireOp",EDGE,"E6.1.0.11")])],"isStart":true})});
            var Q35;
            Q35=makeQuery(id+"F3.boolean.opBoolean","COPY",FACE,{"derivedFrom":makeQuery(id+"F3.opExtrude","CAP_FACE",FACE,{"disambiguationData":[OSD([sQuery(id+"F2.wireOp",EDGE,"E6.2.0.0"),sQuery(id+"F2.wireOp",EDGE,"E6.2.0.4"),sQuery(id+"F2.wireOp",EDGE,"E6.2.0.5"),sQuery(id+"F2.wireOp",EDGE,"E6.2.0.7"),sQuery(id+"F2.wireOp",EDGE,"E6.2.0.8"),sQuery(id+"F2.wireOp",EDGE,"E6.2.0.9"),sQuery(id+"F2.wireOp",EDGE,"E6.2.0.10"),sQuery(id+"F2.wireOp",EDGE,"E6.2.0.11")])],"isStart":true})});
            var Q36;
            Q36=makeQuery(id+"F3.boolean.opBoolean","COPY",FACE,{"derivedFrom":makeQuery(id+"F3.opExtrude","CAP_FACE",FACE,{"disambiguationData":[OSD([sQuery(id+"F2.wireOp",EDGE,"E6.3.0.0"),sQuery(id+"F2.wireOp",EDGE,"E6.3.0.4"),sQuery(id+"F2.wireOp",EDGE,"E6.3.0.5"),sQuery(id+"F2.wireOp",EDGE,"E6.3.0.7"),sQuery(id+"F2.wireOp",EDGE,"E6.3.0.8"),sQuery(id+"F2.wireOp",EDGE,"E6.3.0.9"),sQuery(id+"F2.wireOp",EDGE,"E6.3.0.10"),sQuery(id+"F2.wireOp",EDGE,"E6.3.0.11")])],"isStart":true})});
            var Q37;
            Q37=makeQuery(id+"F3.boolean.opBoolean","COPY",FACE,{"derivedFrom":makeQuery(id+"F3.opExtrude","CAP_FACE",FACE,{"disambiguationData":[OSD([sQuery(id+"F2.wireOp",EDGE,"E6.0.1.0"),sQuery(id+"F2.wireOp",EDGE,"E6.0.1.4"),sQuery(id+"F2.wireOp",EDGE,"E6.0.1.5"),sQuery(id+"F2.wireOp",EDGE,"E6.0.1.7"),sQuery(id+"F2.wireOp",EDGE,"E6.0.1.8"),sQuery(id+"F2.wireOp",EDGE,"E6.0.1.9"),sQuery(id+"F2.wireOp",EDGE,"E6.0.1.10"),sQuery(id+"F2.wireOp",EDGE,"E6.0.1.11")])],"isStart":true})});
            extrude(context, id + "F4", {"entities" : qUnion([Q0, Q1, Q2, Q3, Q4, Q5, Q6, Q7, Q8, Q9, Q10, Q11, Q12, Q13, Q14, Q15, Q16, Q17, Q18, Q19, Q20, Q21, Q22, Q23, Q24, Q25, Q26, Q27, Q28, Q29, Q30, Q31, Q32, Q33, Q34, Q35, Q36, Q37]), "depth" : 0.5 * mm, "offsetDistance" : 25.4 * mm});
        }
        {
            var Q0;
            Q0=makeQuery(id+"F1.opExtrude","CAP_EDGE",EDGE,{"disambiguationData":[OSD([sQuery(id+"F0.wireOp",EDGE,"E0.top")])],"isStart":false});
            var Q1;
            Q1=makeQuery(id+"F1.opExtrude","CAP_EDGE",EDGE,{"disambiguationData":[OSD([sQuery(id+"F0.wireOp",EDGE,"E0.left")])],"isStart":false});
            var Q2;
            Q2=makeQuery(id+"F1.opExtrude","CAP_EDGE",EDGE,{"disambiguationData":[OSD([sQuery(id+"F0.wireOp",EDGE,"E0.right")])],"isStart":false});
            var Q3;
            Q3=makeQuery(id+"F1.opExtrude","CAP_EDGE",EDGE,{"disambiguationData":[OSD([sQuery(id+"F0.wireOp",EDGE,"E0.bottom")])],"isStart":false});
            fillet(context, id + "F5", {"entities" : qUnion([Q0, Q1, Q2, Q3]), "radius" : 1.27 * mm, "tangentPropagation" : true, "allowEdgeOverflow" : false});
        }
        {
            var Q0;
            Q0=makeQuery(id+"F4.opExtrude","SWEPT_BODY",BODY,{"disambiguationData":[OSD([sQuery(id+"F2.wireOp",EDGE,"E1.bottom"),sQuery(id+"F2.wireOp",EDGE,"E1.top"),sQuery(id+"F2.wireOp",EDGE,"E1.left"),sQuery(id+"F2.wireOp",EDGE,"E1.right"),sQuery(id+"F2.wireOp",EDGE,"E2.filletArc"),sQuery(id+"F2.wireOp",EDGE,"E3.filletArc"),sQuery(id+"F2.wireOp",EDGE,"E4.filletArc"),sQuery(id+"F2.wireOp",EDGE,"E5.filletArc")])]});
            var Q1;
            Q1=makeQuery(id+"F4.opExtrude","SWEPT_BODY",BODY,{"disambiguationData":[OSD([sQuery(id+"F2.wireOp",EDGE,"E6.0.1.0"),sQuery(id+"F2.wireOp",EDGE,"E6.0.1.4"),sQuery(id+"F2.wireOp",EDGE,"E6.0.1.5"),sQuery(id+"F2.wireOp",EDGE,"E6.0.1.7"),sQuery(id+"F2.wireOp",EDGE,"E6.0.1.8"),sQuery(id+"F2.wireOp",EDGE,"E6.0.1.9"),sQuery(id+"F2.wireOp",EDGE,"E6.0.1.10"),sQuery(id+"F2.wireOp",EDGE,"E6.0.1.11")])]});
            var Q2;
            Q2=makeQuery(id+"F4.opExtrude","SWEPT_BODY",BODY,{"disambiguationData":[OSD([sQuery(id+"F2.wireOp",EDGE,"E6.0.2.0"),sQuery(id+"F2.wireOp",EDGE,"E6.0.2.4"),sQuery(id+"F2.wireOp",EDGE,"E6.0.2.5"),sQuery(id+"F2.wireOp",EDGE,"E6.0.2.7"),sQuery(id+"F2.wireOp",EDGE,"E6.0.2.8"),sQuery(id+"F2.wireOp",EDGE,"E6.0.2.9"),sQuery(id+"F2.wireOp",EDGE,"E6.0.2.10"),sQuery(id+"F2.wireOp",EDGE,"E6.0.2.11")])]});
            var Q3;
            Q3=makeQuery(id+"F4.opExtrude","SWEPT_BODY",BODY,{"disambiguationData":[OSD([sQuery(id+"F2.wireOp",EDGE,"E6.0.3.0"),sQuery(id+"F2.wireOp",EDGE,"E6.0.3.4"),sQuery(id+"F2.wireOp",EDGE,"E6.0.3.5"),sQuery(id+"F2.wireOp",EDGE,"E6.0.3.7"),sQuery(id+"F2.wireOp",EDGE,"E6.0.3.8"),sQuery(id+"F2.wireOp",EDGE,"E6.0.3.9"),sQuery(id+"F2.wireOp",EDGE,"E6.0.3.10"),sQuery(id+"F2.wireOp",EDGE,"E6.0.3.11")])]});
            var Q4;
            Q4=makeQuery(id+"F4.opExtrude","SWEPT_BODY",BODY,{"disambiguationData":[OSD([sQuery(id+"F2.wireOp",EDGE,"E6.0.4.0"),sQuery(id+"F2.wireOp",EDGE,"E6.0.4.4"),sQuery(id+"F2.wireOp",EDGE,"E6.0.4.5"),sQuery(id+"F2.wireOp",EDGE,"E6.0.4.7"),sQuery(id+"F2.wireOp",EDGE,"E6.0.4.8"),sQuery(id+"F2.wireOp",EDGE,"E6.0.4.9"),sQuery(id+"F2.wireOp",EDGE,"E6.0.4.10"),sQuery(id+"F2.wireOp",EDGE,"E6.0.4.11")])]});
            var Q5;
            Q5=makeQuery(id+"F4.opExtrude","SWEPT_BODY",BODY,{"disambiguationData":[OSD([sQuery(id+"F2.wireOp",EDGE,"E6.0.5.0"),sQuery(id+"F2.wireOp",EDGE,"E6.0.5.4"),sQuery(id+"F2.wireOp",EDGE,"E6.0.5.5"),sQuery(id+"F2.wireOp",EDGE,"E6.0.5.7"),sQuery(id+"F2.wireOp",EDGE,"E6.0.5.8"),sQuery(id+"F2.wireOp",EDGE,"E6.0.5.9"),sQuery(id+"F2.wireOp",EDGE,"E6.0.5.10"),sQuery(id+"F2.wireOp",EDGE,"E6.0.5.11")])]});
            var Q6;
            Q6=makeQuery(id+"F4.opExtrude","SWEPT_BODY",BODY,{"disambiguationData":[OSD([sQuery(id+"F2.wireOp",EDGE,"E6.0.6.0"),sQuery(id+"F2.wireOp",EDGE,"E6.0.6.4"),sQuery(id+"F2.wireOp",EDGE,"E6.0.6.5"),sQuery(id+"F2.wireOp",EDGE,"E6.0.6.7"),sQuery(id+"F2.wireOp",EDGE,"E6.0.6.8"),sQuery(id+"F2.wireOp",EDGE,"E6.0.6.9"),sQuery(id+"F2.wireOp",EDGE,"E6.0.6.10"),sQuery(id+"F2.wireOp",EDGE,"E6.0.6.11")])]});
            var Q7;
            Q7=makeQuery(id+"F4.opExtrude","SWEPT_BODY",BODY,{"disambiguationData":[OSD([sQuery(id+"F2.wireOp",EDGE,"E6.0.7.0"),sQuery(id+"F2.wireOp",EDGE,"E6.0.7.4"),sQuery(id+"F2.wireOp",EDGE,"E6.0.7.5"),sQuery(id+"F2.wireOp",EDGE,"E6.0.7.7"),sQuery(id+"F2.wireOp",EDGE,"E6.0.7.8"),sQuery(id+"F2.wireOp",EDGE,"E6.0.7.9"),sQuery(id+"F2.wireOp",EDGE,"E6.0.7.10"),sQuery(id+"F2.wireOp",EDGE,"E6.0.7.11")])]});
            var Q8;
            Q8=makeQuery(id+"F4.opExtrude","SWEPT_BODY",BODY,{"disambiguationData":[OSD([sQuery(id+"F2.wireOp",EDGE,"E6.0.8.0"),sQuery(id+"F2.wireOp",EDGE,"E6.0.8.4"),sQuery(id+"F2.wireOp",EDGE,"E6.0.8.5"),sQuery(id+"F2.wireOp",EDGE,"E6.0.8.7"),sQuery(id+"F2.wireOp",EDGE,"E6.0.8.8"),sQuery(id+"F2.wireOp",EDGE,"E6.0.8.9"),sQuery(id+"F2.wireOp",EDGE,"E6.0.8.10"),sQuery(id+"F2.wireOp",EDGE,"E6.0.8.11")])]});
            var Q9;
            Q9=makeQuery(id+"F4.opExtrude","SWEPT_BODY",BODY,{"disambiguationData":[OSD([sQuery(id+"F2.wireOp",EDGE,"E6.1.0.0"),sQuery(id+"F2.wireOp",EDGE,"E6.1.0.4"),sQuery(id+"F2.wireOp",EDGE,"E6.1.0.5"),sQuery(id+"F2.wireOp",EDGE,"E6.1.0.7"),sQuery(id+"F2.wireOp",EDGE,"E6.1.0.8"),sQuery(id+"F2.wireOp",EDGE,"E6.1.0.9"),sQuery(id+"F2.wireOp",EDGE,"E6.1.0.10"),sQuery(id+"F2.wireOp",EDGE,"E6.1.0.11")])]});
            var Q10;
            Q10=makeQuery(id+"F4.opExtrude","SWEPT_BODY",BODY,{"disambiguationData":[OSD([sQuery(id+"F2.wireOp",EDGE,"E6.1.1.0"),sQuery(id+"F2.wireOp",EDGE,"E6.1.1.4"),sQuery(id+"F2.wireOp",EDGE,"E6.1.1.5"),sQuery(id+"F2.wireOp",EDGE,"E6.1.1.7"),sQuery(id+"F2.wireOp",EDGE,"E6.1.1.8"),sQuery(id+"F2.wireOp",EDGE,"E6.1.1.9"),sQuery(id+"F2.wireOp",EDGE,"E6.1.1.10"),sQuery(id+"F2.wireOp",EDGE,"E6.1.1.11")])]});
            var Q11;
            Q11=makeQuery(id+"F4.opExtrude","SWEPT_BODY",BODY,{"disambiguationData":[OSD([sQuery(id+"F2.wireOp",EDGE,"E6.1.2.0"),sQuery(id+"F2.wireOp",EDGE,"E6.1.2.4"),sQuery(id+"F2.wireOp",EDGE,"E6.1.2.5"),sQuery(id+"F2.wireOp",EDGE,"E6.1.2.7"),sQuery(id+"F2.wireOp",EDGE,"E6.1.2.8"),sQuery(id+"F2.wireOp",EDGE,"E6.1.2.9"),sQuery(id+"F2.wireOp",EDGE,"E6.1.2.10"),sQuery(id+"F2.wireOp",EDGE,"E6.1.2.11")])]});
            var Q12;
            Q12=makeQuery(id+"F4.opExtrude","SWEPT_BODY",BODY,{"disambiguationData":[OSD([sQuery(id+"F2.wireOp",EDGE,"E6.1.3.0"),sQuery(id+"F2.wireOp",EDGE,"E6.1.3.4"),sQuery(id+"F2.wireOp",EDGE,"E6.1.3.5"),sQuery(id+"F2.wireOp",EDGE,"E6.1.3.7"),sQuery(id+"F2.wireOp",EDGE,"E6.1.3.8"),sQuery(id+"F2.wireOp",EDGE,"E6.1.3.9"),sQuery(id+"F2.wireOp",EDGE,"E6.1.3.10"),sQuery(id+"F2.wireOp",EDGE,"E6.1.3.11")])]});
            var Q13;
            Q13=makeQuery(id+"F4.opExtrude","SWEPT_BODY",BODY,{"disambiguationData":[OSD([sQuery(id+"F2.wireOp",EDGE,"E6.1.4.0"),sQuery(id+"F2.wireOp",EDGE,"E6.1.4.4"),sQuery(id+"F2.wireOp",EDGE,"E6.1.4.5"),sQuery(id+"F2.wireOp",EDGE,"E6.1.4.7"),sQuery(id+"F2.wireOp",EDGE,"E6.1.4.8"),sQuery(id+"F2.wireOp",EDGE,"E6.1.4.9"),sQuery(id+"F2.wireOp",EDGE,"E6.1.4.10"),sQuery(id+"F2.wireOp",EDGE,"E6.1.4.11")])]});
            var Q14;
            Q14=makeQuery(id+"F4.opExtrude","SWEPT_BODY",BODY,{"disambiguationData":[OSD([sQuery(id+"F2.wireOp",EDGE,"E6.1.5.0"),sQuery(id+"F2.wireOp",EDGE,"E6.1.5.4"),sQuery(id+"F2.wireOp",EDGE,"E6.1.5.5"),sQuery(id+"F2.wireOp",EDGE,"E6.1.5.7"),sQuery(id+"F2.wireOp",EDGE,"E6.1.5.8"),sQuery(id+"F2.wireOp",EDGE,"E6.1.5.9"),sQuery(id+"F2.wireOp",EDGE,"E6.1.5.10"),sQuery(id+"F2.wireOp",EDGE,"E6.1.5.11")])]});
            var Q15;
            Q15=makeQuery(id+"F4.opExtrude","SWEPT_BODY",BODY,{"disambiguationData":[OSD([sQuery(id+"F2.wireOp",EDGE,"E6.1.6.0"),sQuery(id+"F2.wireOp",EDGE,"E6.1.6.4"),sQuery(id+"F2.wireOp",EDGE,"E6.1.6.5"),sQuery(id+"F2.wireOp",EDGE,"E6.1.6.7"),sQuery(id+"F2.wireOp",EDGE,"E6.1.6.8"),sQuery(id+"F2.wireOp",EDGE,"E6.1.6.9"),sQuery(id+"F2.wireOp",EDGE,"E6.1.6.10"),sQuery(id+"F2.wireOp",EDGE,"E6.1.6.11")])]});
            var Q16;
            Q16=makeQuery(id+"F4.opExtrude","SWEPT_BODY",BODY,{"disambiguationData":[OSD([sQuery(id+"F2.wireOp",EDGE,"E6.1.7.0"),sQuery(id+"F2.wireOp",EDGE,"E6.1.7.4"),sQuery(id+"F2.wireOp",EDGE,"E6.1.7.5"),sQuery(id+"F2.wireOp",EDGE,"E6.1.7.7"),sQuery(id+"F2.wireOp",EDGE,"E6.1.7.8"),sQuery(id+"F2.wireOp",EDGE,"E6.1.7.9"),sQuery(id+"F2.wireOp",EDGE,"E6.1.7.10"),sQuery(id+"F2.wireOp",EDGE,"E6.1.7.11")])]});
            var Q17;
            Q17=makeQuery(id+"F4.opExtrude","SWEPT_BODY",BODY,{"disambiguationData":[OSD([sQuery(id+"F2.wireOp",EDGE,"E6.1.8.0"),sQuery(id+"F2.wireOp",EDGE,"E6.1.8.4"),sQuery(id+"F2.wireOp",EDGE,"E6.1.8.5"),sQuery(id+"F2.wireOp",EDGE,"E6.1.8.7"),sQuery(id+"F2.wireOp",EDGE,"E6.1.8.8"),sQuery(id+"F2.wireOp",EDGE,"E6.1.8.9"),sQuery(id+"F2.wireOp",EDGE,"E6.1.8.10"),sQuery(id+"F2.wireOp",EDGE,"E6.1.8.11")])]});
            var Q18;
            Q18=makeQuery(id+"F4.opExtrude","SWEPT_BODY",BODY,{"disambiguationData":[OSD([sQuery(id+"F2.wireOp",EDGE,"E6.2.0.0"),sQuery(id+"F2.wireOp",EDGE,"E6.2.0.4"),sQuery(id+"F2.wireOp",EDGE,"E6.2.0.5"),sQuery(id+"F2.wireOp",EDGE,"E6.2.0.7"),sQuery(id+"F2.wireOp",EDGE,"E6.2.0.8"),sQuery(id+"F2.wireOp",EDGE,"E6.2.0.9"),sQuery(id+"F2.wireOp",EDGE,"E6.2.0.10"),sQuery(id+"F2.wireOp",EDGE,"E6.2.0.11")])]});
            var Q19;
            Q19=makeQuery(id+"F4.opExtrude","SWEPT_BODY",BODY,{"disambiguationData":[OSD([sQuery(id+"F2.wireOp",EDGE,"E6.2.1.0"),sQuery(id+"F2.wireOp",EDGE,"E6.2.1.4"),sQuery(id+"F2.wireOp",EDGE,"E6.2.1.5"),sQuery(id+"F2.wireOp",EDGE,"E6.2.1.7"),sQuery(id+"F2.wireOp",EDGE,"E6.2.1.8"),sQuery(id+"F2.wireOp",EDGE,"E6.2.1.9"),sQuery(id+"F2.wireOp",EDGE,"E6.2.1.10"),sQuery(id+"F2.wireOp",EDGE,"E6.2.1.11")])]});
            var Q20;
            Q20=makeQuery(id+"F4.opExtrude","SWEPT_BODY",BODY,{"disambiguationData":[OSD([sQuery(id+"F2.wireOp",EDGE,"E6.2.2.0"),sQuery(id+"F2.wireOp",EDGE,"E6.2.2.4"),sQuery(id+"F2.wireOp",EDGE,"E6.2.2.5"),sQuery(id+"F2.wireOp",EDGE,"E6.2.2.7"),sQuery(id+"F2.wireOp",EDGE,"E6.2.2.8"),sQuery(id+"F2.wireOp",EDGE,"E6.2.2.9"),sQuery(id+"F2.wireOp",EDGE,"E6.2.2.10"),sQuery(id+"F2.wireOp",EDGE,"E6.2.2.11")])]});
            var Q21;
            Q21=makeQuery(id+"F4.opExtrude","SWEPT_BODY",BODY,{"disambiguationData":[OSD([sQuery(id+"F2.wireOp",EDGE,"E6.2.3.0"),sQuery(id+"F2.wireOp",EDGE,"E6.2.3.4"),sQuery(id+"F2.wireOp",EDGE,"E6.2.3.5"),sQuery(id+"F2.wireOp",EDGE,"E6.2.3.7"),sQuery(id+"F2.wireOp",EDGE,"E6.2.3.8"),sQuery(id+"F2.wireOp",EDGE,"E6.2.3.9"),sQuery(id+"F2.wireOp",EDGE,"E6.2.3.10"),sQuery(id+"F2.wireOp",EDGE,"E6.2.3.11")])]});
            var Q22;
            Q22=makeQuery(id+"F4.opExtrude","SWEPT_BODY",BODY,{"disambiguationData":[OSD([sQuery(id+"F2.wireOp",EDGE,"E6.2.4.0"),sQuery(id+"F2.wireOp",EDGE,"E6.2.4.4"),sQuery(id+"F2.wireOp",EDGE,"E6.2.4.5"),sQuery(id+"F2.wireOp",EDGE,"E6.2.4.7"),sQuery(id+"F2.wireOp",EDGE,"E6.2.4.8"),sQuery(id+"F2.wireOp",EDGE,"E6.2.4.9"),sQuery(id+"F2.wireOp",EDGE,"E6.2.4.10"),sQuery(id+"F2.wireOp",EDGE,"E6.2.4.11")])]});
            var Q23;
            Q23=makeQuery(id+"F4.opExtrude","SWEPT_BODY",BODY,{"disambiguationData":[OSD([sQuery(id+"F2.wireOp",EDGE,"E6.2.5.0"),sQuery(id+"F2.wireOp",EDGE,"E6.2.5.4"),sQuery(id+"F2.wireOp",EDGE,"E6.2.5.5"),sQuery(id+"F2.wireOp",EDGE,"E6.2.5.7"),sQuery(id+"F2.wireOp",EDGE,"E6.2.5.8"),sQuery(id+"F2.wireOp",EDGE,"E6.2.5.9"),sQuery(id+"F2.wireOp",EDGE,"E6.2.5.10"),sQuery(id+"F2.wireOp",EDGE,"E6.2.5.11")])]});
            var Q24;
            Q24=makeQuery(id+"F4.opExtrude","SWEPT_BODY",BODY,{"disambiguationData":[OSD([sQuery(id+"F2.wireOp",EDGE,"E6.2.6.0"),sQuery(id+"F2.wireOp",EDGE,"E6.2.6.4"),sQuery(id+"F2.wireOp",EDGE,"E6.2.6.5"),sQuery(id+"F2.wireOp",EDGE,"E6.2.6.7"),sQuery(id+"F2.wireOp",EDGE,"E6.2.6.8"),sQuery(id+"F2.wireOp",EDGE,"E6.2.6.9"),sQuery(id+"F2.wireOp",EDGE,"E6.2.6.10"),sQuery(id+"F2.wireOp",EDGE,"E6.2.6.11")])]});
            var Q25;
            Q25=makeQuery(id+"F4.opExtrude","SWEPT_BODY",BODY,{"disambiguationData":[OSD([sQuery(id+"F2.wireOp",EDGE,"E6.2.7.0"),sQuery(id+"F2.wireOp",EDGE,"E6.2.7.4"),sQuery(id+"F2.wireOp",EDGE,"E6.2.7.5"),sQuery(id+"F2.wireOp",EDGE,"E6.2.7.7"),sQuery(id+"F2.wireOp",EDGE,"E6.2.7.8"),sQuery(id+"F2.wireOp",EDGE,"E6.2.7.9"),sQuery(id+"F2.wireOp",EDGE,"E6.2.7.10"),sQuery(id+"F2.wireOp",EDGE,"E6.2.7.11")])]});
            var Q26;
            Q26=makeQuery(id+"F4.opExtrude","SWEPT_BODY",BODY,{"disambiguationData":[OSD([sQuery(id+"F2.wireOp",EDGE,"E6.2.8.0"),sQuery(id+"F2.wireOp",EDGE,"E6.2.8.4"),sQuery(id+"F2.wireOp",EDGE,"E6.2.8.5"),sQuery(id+"F2.wireOp",EDGE,"E6.2.8.7"),sQuery(id+"F2.wireOp",EDGE,"E6.2.8.8"),sQuery(id+"F2.wireOp",EDGE,"E6.2.8.9"),sQuery(id+"F2.wireOp",EDGE,"E6.2.8.10"),sQuery(id+"F2.wireOp",EDGE,"E6.2.8.11")])]});
            var Q27;
            Q27=makeQuery(id+"F4.opExtrude","SWEPT_BODY",BODY,{"disambiguationData":[OSD([sQuery(id+"F2.wireOp",EDGE,"E6.3.0.0"),sQuery(id+"F2.wireOp",EDGE,"E6.3.0.4"),sQuery(id+"F2.wireOp",EDGE,"E6.3.0.5"),sQuery(id+"F2.wireOp",EDGE,"E6.3.0.7"),sQuery(id+"F2.wireOp",EDGE,"E6.3.0.8"),sQuery(id+"F2.wireOp",EDGE,"E6.3.0.9"),sQuery(id+"F2.wireOp",EDGE,"E6.3.0.10"),sQuery(id+"F2.wireOp",EDGE,"E6.3.0.11")])]});
            var Q28;
            Q28=makeQuery(id+"F4.opExtrude","SWEPT_BODY",BODY,{"disambiguationData":[OSD([sQuery(id+"F2.wireOp",EDGE,"E6.3.1.0"),sQuery(id+"F2.wireOp",EDGE,"E6.3.1.4"),sQuery(id+"F2.wireOp",EDGE,"E6.3.1.5"),sQuery(id+"F2.wireOp",EDGE,"E6.3.1.7"),sQuery(id+"F2.wireOp",EDGE,"E6.3.1.8"),sQuery(id+"F2.wireOp",EDGE,"E6.3.1.9"),sQuery(id+"F2.wireOp",EDGE,"E6.3.1.10"),sQuery(id+"F2.wireOp",EDGE,"E6.3.1.11")])]});
            var Q29;
            Q29=makeQuery(id+"F4.opExtrude","SWEPT_BODY",BODY,{"disambiguationData":[OSD([sQuery(id+"F2.wireOp",EDGE,"E6.3.2.0"),sQuery(id+"F2.wireOp",EDGE,"E6.3.2.4"),sQuery(id+"F2.wireOp",EDGE,"E6.3.2.5"),sQuery(id+"F2.wireOp",EDGE,"E6.3.2.7"),sQuery(id+"F2.wireOp",EDGE,"E6.3.2.8"),sQuery(id+"F2.wireOp",EDGE,"E6.3.2.9"),sQuery(id+"F2.wireOp",EDGE,"E6.3.2.10"),sQuery(id+"F2.wireOp",EDGE,"E6.3.2.11")])]});
            var Q30;
            Q30=makeQuery(id+"F4.opExtrude","SWEPT_BODY",BODY,{"disambiguationData":[OSD([sQuery(id+"F2.wireOp",EDGE,"E6.3.3.0"),sQuery(id+"F2.wireOp",EDGE,"E6.3.3.4"),sQuery(id+"F2.wireOp",EDGE,"E6.3.3.5"),sQuery(id+"F2.wireOp",EDGE,"E6.3.3.7"),sQuery(id+"F2.wireOp",EDGE,"E6.3.3.8"),sQuery(id+"F2.wireOp",EDGE,"E6.3.3.9"),sQuery(id+"F2.wireOp",EDGE,"E6.3.3.10"),sQuery(id+"F2.wireOp",EDGE,"E6.3.3.11")])]});
            var Q31;
            Q31=makeQuery(id+"F4.opExtrude","SWEPT_BODY",BODY,{"disambiguationData":[OSD([sQuery(id+"F2.wireOp",EDGE,"E6.3.4.0"),sQuery(id+"F2.wireOp",EDGE,"E6.3.4.4"),sQuery(id+"F2.wireOp",EDGE,"E6.3.4.5"),sQuery(id+"F2.wireOp",EDGE,"E6.3.4.7"),sQuery(id+"F2.wireOp",EDGE,"E6.3.4.8"),sQuery(id+"F2.wireOp",EDGE,"E6.3.4.9"),sQuery(id+"F2.wireOp",EDGE,"E6.3.4.10"),sQuery(id+"F2.wireOp",EDGE,"E6.3.4.11")])]});
            var Q32;
            Q32=makeQuery(id+"F4.opExtrude","SWEPT_BODY",BODY,{"disambiguationData":[OSD([sQuery(id+"F2.wireOp",EDGE,"E6.3.5.0"),sQuery(id+"F2.wireOp",EDGE,"E6.3.5.4"),sQuery(id+"F2.wireOp",EDGE,"E6.3.5.5"),sQuery(id+"F2.wireOp",EDGE,"E6.3.5.7"),sQuery(id+"F2.wireOp",EDGE,"E6.3.5.8"),sQuery(id+"F2.wireOp",EDGE,"E6.3.5.9"),sQuery(id+"F2.wireOp",EDGE,"E6.3.5.10"),sQuery(id+"F2.wireOp",EDGE,"E6.3.5.11")])]});
            var Q33;
            Q33=makeQuery(id+"F4.opExtrude","SWEPT_BODY",BODY,{"disambiguationData":[OSD([sQuery(id+"F2.wireOp",EDGE,"E6.3.6.0"),sQuery(id+"F2.wireOp",EDGE,"E6.3.6.4"),sQuery(id+"F2.wireOp",EDGE,"E6.3.6.5"),sQuery(id+"F2.wireOp",EDGE,"E6.3.6.7"),sQuery(id+"F2.wireOp",EDGE,"E6.3.6.8"),sQuery(id+"F2.wireOp",EDGE,"E6.3.6.9"),sQuery(id+"F2.wireOp",EDGE,"E6.3.6.10"),sQuery(id+"F2.wireOp",EDGE,"E6.3.6.11")])]});
            var Q34;
            Q34=makeQuery(id+"F4.opExtrude","SWEPT_BODY",BODY,{"disambiguationData":[OSD([sQuery(id+"F2.wireOp",EDGE,"E6.3.7.0"),sQuery(id+"F2.wireOp",EDGE,"E6.3.7.4"),sQuery(id+"F2.wireOp",EDGE,"E6.3.7.5"),sQuery(id+"F2.wireOp",EDGE,"E6.3.7.7"),sQuery(id+"F2.wireOp",EDGE,"E6.3.7.8"),sQuery(id+"F2.wireOp",EDGE,"E6.3.7.9"),sQuery(id+"F2.wireOp",EDGE,"E6.3.7.10"),sQuery(id+"F2.wireOp",EDGE,"E6.3.7.11")])]});
            var Q35;
            Q35=makeQuery(id+"F4.opExtrude","SWEPT_BODY",BODY,{"disambiguationData":[OSD([sQuery(id+"F2.wireOp",EDGE,"E6.3.8.0"),sQuery(id+"F2.wireOp",EDGE,"E6.3.8.4"),sQuery(id+"F2.wireOp",EDGE,"E6.3.8.5"),sQuery(id+"F2.wireOp",EDGE,"E6.3.8.7"),sQuery(id+"F2.wireOp",EDGE,"E6.3.8.8"),sQuery(id+"F2.wireOp",EDGE,"E6.3.8.9"),sQuery(id+"F2.wireOp",EDGE,"E6.3.8.10"),sQuery(id+"F2.wireOp",EDGE,"E6.3.8.11")])]});
            deleteBodies(context, id + "F6", {"entities" : qUnion([Q0, Q1, Q2, Q3, Q4, Q5, Q6, Q7, Q8, Q9, Q10, Q11, Q12, Q13, Q14, Q15, Q16, Q17, Q18, Q19, Q20, Q21, Q22, Q23, Q24, Q25, Q26, Q27, Q28, Q29, Q30, Q31, Q32, Q33, Q34, Q35])});
        }
    });
